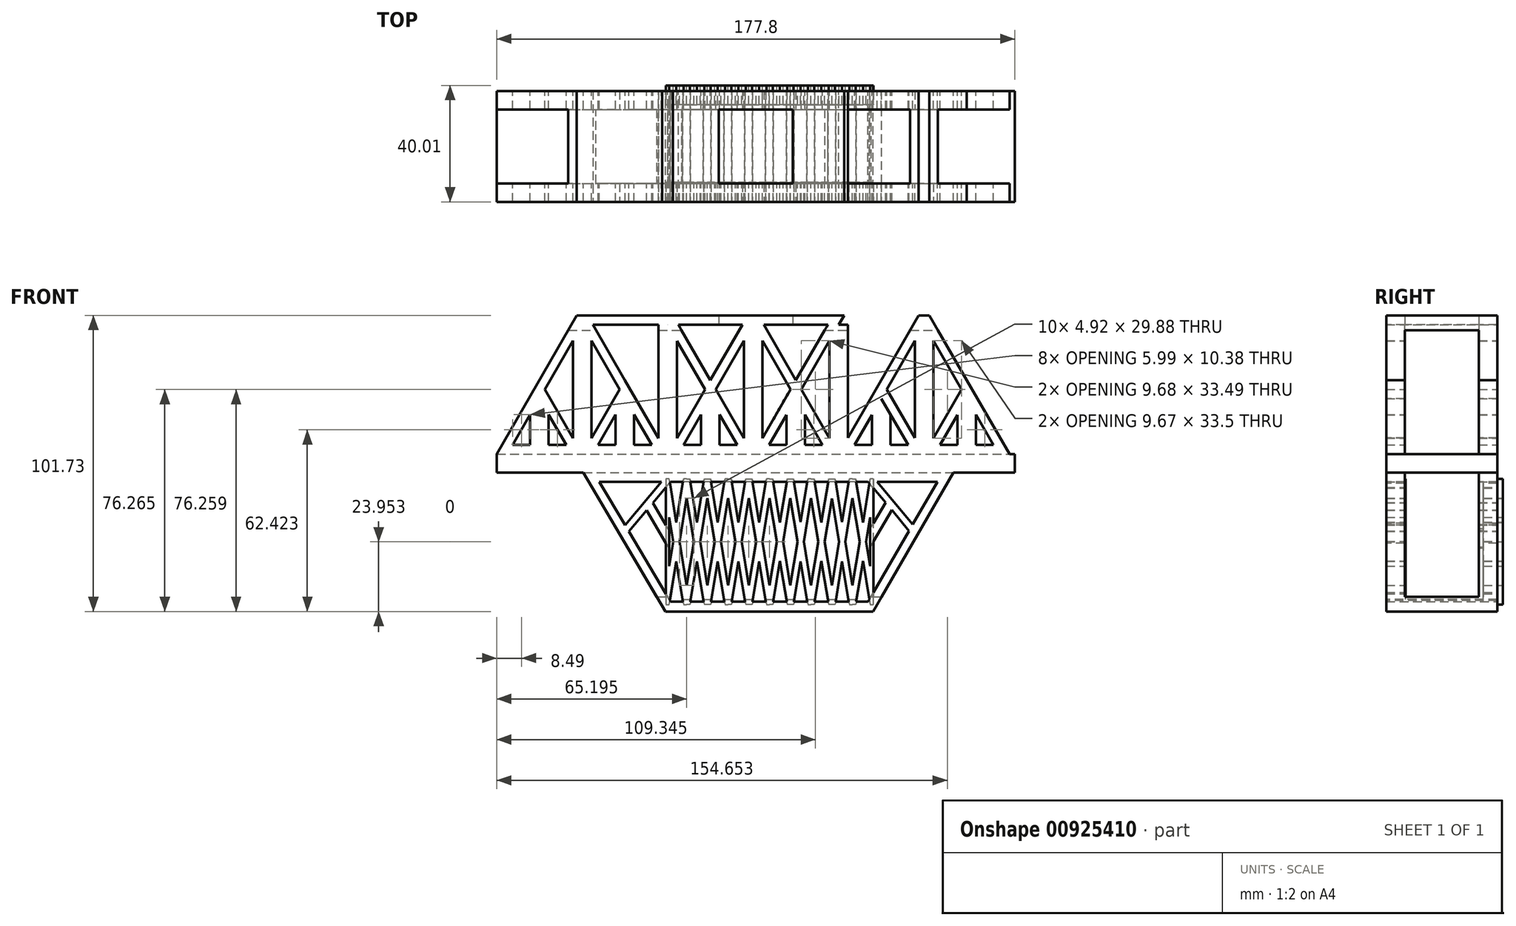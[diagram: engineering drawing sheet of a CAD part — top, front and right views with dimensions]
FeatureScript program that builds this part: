
annotation { "Feature Type Name" : "Feature", "Feature Type Description" : "" }
export const myFeature = defineFeature(function(context is Context, id is Id, definition is map)
    precondition{}
    {
        {
            var Q0;
            Q0=qCreatedBy(makeId("Front.planeOp"),FACE);
            var sketch = newSketch(context, id + "F0", { "sketchPlane" : qUnion([Q0])});
            skLineSegment(sketch, "E0.0.11", {"start": v(-111.17, 12.7) * mm, "end": v(-111.17, 0) * mm});
            skLineSegment(sketch, "E0.0.13", {"start": v(66.63, 0) * mm, "end": v(66.63, 12.7) * mm});
            skLineSegment(sketch, "E1", {"start": v(-111.17, 12.7) * mm, "end": v(66.63, 12.7) * mm});
            skLineSegment(sketch, "E2", {"start": v(66.63, 0) * mm, "end": v(-111.17, 0) * mm});
            skSolve(sketch);
        }
        {
            var Q0;
            Q0=qCreatedBy(makeId("Front.planeOp"),FACE);
            var sketch = newSketch(context, id + "F1", { "sketchPlane" : qUnion([Q0])});
            skLineSegment(sketch, "E3", {"start": v(-111.17, 0) * mm, "end": v(66.63, 0) * mm});
            skLineSegment(sketch, "E4", {"start": v(-111.17, 0) * mm, "end": v(-111.17, 12.7) * mm});
            skLineSegment(sketch, "E5", {"start": v(66.63, 12.7) * mm, "end": v(66.63, 0) * mm});
            skLineSegment(sketch, "E6", {"start": v(-111.17, 63.7) * mm, "end": v(-111.17, -37.9) * mm, "construction": true});
            skPoint(sketch, "E7.0.midPoint", {"position": v(-99.44, 28.1) * mm});
            skCircle(sketch, "E8.cCircle", {"center": v(-96.5, 21.17) * mm, "radius": 8.47 * mm, "construction": true});
            skLineSegment(sketch, "E8.0", {"start": v(-81.85, 12.7) * mm, "end": v(-111.17, 12.7) * mm});
            skLineSegment(sketch, "E8.1", {"start": v(-111.17, 12.7) * mm, "end": v(-96.5, 38.1) * mm});
            skLineSegment(sketch, "E8.2", {"start": v(-96.5, 38.1) * mm, "end": v(-81.85, 12.7) * mm});
            skLineSegment(sketch, "E9", {"start": v(-96.5, 38.1) * mm, "end": v(-96.5, 31.75) * mm, "construction": true});
            skCircle(sketch, "E10.cCircle", {"center": v(-96.5, 21.17) * mm, "radius": 5.3 * mm, "construction": true});
            skLineSegment(sketch, "E10.0", {"start": v(-87.34, 15.88) * mm, "end": v(-105.68, 15.88) * mm});
            skLineSegment(sketch, "E10.1", {"start": v(-105.68, 15.87) * mm, "end": v(-96.5, 31.75) * mm});
            skLineSegment(sketch, "E10.2", {"start": v(-96.5, 31.75) * mm, "end": v(-87.34, 15.88) * mm});
            skPoint(sketch, "E10.0.midPoint", {"position": v(-96.5, 15.88) * mm});
            skLineSegment(sketch, "E11", {"start": v(66.63, 12.7) * mm, "end": v(-111.17, 12.7) * mm});
            skLineSegment(sketch, "E12.direction1", {"start": v(-111.17, 12.7) * mm, "end": v(-81.85, 12.7) * mm, "construction": true});
            skLineSegment(sketch, "E13", {"start": v(-96.5, 38.1) * mm, "end": v(-96.5, 12.7) * mm, "construction": true});
            skLineSegment(sketch, "E14", {"start": v(-96.5, 31.75) * mm, "end": v(-93.33, 31.75) * mm, "construction": true});
            skLineSegment(sketch, "E15", {"start": v(-96.5, 31.75) * mm, "end": v(-99.68, 31.75) * mm, "construction": true});
            skLineSegment(sketch, "E16", {"start": v(-99.68, 31.75) * mm, "end": v(-99.68, 26.25) * mm, "construction": true});
            skLineSegment(sketch, "E17", {"start": v(-93.33, 31.75) * mm, "end": v(-93.33, 26.25) * mm, "construction": true});
            skLineSegment(sketch, "E18", {"start": v(-99.68, 26.25) * mm, "end": v(-99.68, 15.88) * mm});
            skLineSegment(sketch, "E19", {"start": v(-93.33, 26.25) * mm, "end": v(-93.33, 15.88) * mm});
            skLineSegment(sketch, "E20.1.0.0", {"start": v(-58, 15.88) * mm, "end": v(-76.34, 15.88) * mm});
            skLineSegment(sketch, "E20.1.0.1", {"start": v(-70.35, 26.25) * mm, "end": v(-70.35, 15.88) * mm});
            skLineSegment(sketch, "E20.1.0.2", {"start": v(-67.17, 38.1) * mm, "end": v(-52.5, 12.7) * mm});
            skPoint(sketch, "E20.1.0.3", {"position": v(-67.17, 15.88) * mm});
            skLineSegment(sketch, "E20.1.0.4", {"start": v(-67.17, 31.75) * mm, "end": v(-58, 15.88) * mm});
            skCircle(sketch, "E20.1.0.5", {"center": v(-67.17, 21.17) * mm, "radius": 8.47 * mm, "construction": true});
            skPoint(sketch, "E20.1.0.6", {"position": v(-70.1, 28.1) * mm});
            skLineSegment(sketch, "E20.1.0.7", {"start": v(-64, 26.25) * mm, "end": v(-64, 15.88) * mm});
            skLineSegment(sketch, "E20.1.0.8", {"start": v(-81.84, 12.7) * mm, "end": v(-52.5, 12.7) * mm, "construction": true});
            skLineSegment(sketch, "E20.1.0.9", {"start": v(-76.34, 15.87) * mm, "end": v(-67.17, 31.75) * mm});
            skCircle(sketch, "E20.1.0.10", {"center": v(-67.17, 21.17) * mm, "radius": 5.3 * mm, "construction": true});
            skLineSegment(sketch, "E20.1.0.11", {"start": v(-81.84, 12.7) * mm, "end": v(-67.17, 38.1) * mm});
            skLineSegment(sketch, "E20.1.0.12", {"start": v(-64, 31.75) * mm, "end": v(-64, 26.25) * mm, "construction": true});
            skLineSegment(sketch, "E20.1.0.13", {"start": v(-67.17, 38.1) * mm, "end": v(-67.17, 12.7) * mm, "construction": true});
            skLineSegment(sketch, "E20.1.0.14", {"start": v(-52.5, 12.7) * mm, "end": v(-81.84, 12.7) * mm});
            skLineSegment(sketch, "E20.1.0.15", {"start": v(-67.17, 38.1) * mm, "end": v(-67.17, 31.75) * mm, "construction": true});
            skLineSegment(sketch, "E20.1.0.16", {"start": v(-70.35, 31.75) * mm, "end": v(-70.35, 26.25) * mm, "construction": true});
            skLineSegment(sketch, "E20.1.0.17", {"start": v(-67.17, 31.75) * mm, "end": v(-70.35, 31.75) * mm, "construction": true});
            skLineSegment(sketch, "E20.1.0.18", {"start": v(-67.17, 31.75) * mm, "end": v(-64, 31.75) * mm, "construction": true});
            skLineSegment(sketch, "E20.direction1", {"start": v(-111.17, 12.7) * mm, "end": v(-81.84, 12.7) * mm, "construction": true});
            skLineSegment(sketch, "E21", {"start": v(-52.5, 12.7) * mm, "end": v(-52.5, 29.72) * mm, "construction": true});
            skLineSegment(sketch, "E22.MirrorCS", {"start": v(-37.84, 31.75) * mm, "end": v(-34.67, 31.75) * mm, "construction": true});
            skLineSegment(sketch, "E23.MirrorCS", {"start": v(-37.84, 31.75) * mm, "end": v(-41.02, 31.75) * mm, "construction": true});
            skLineSegment(sketch, "E24.MirrorCS", {"start": v(-37.84, 38.1) * mm, "end": v(-37.84, 31.75) * mm, "construction": true});
            skLineSegment(sketch, "E25.MirrorCS", {"start": v(-34.67, 31.75) * mm, "end": v(-34.67, 26.25) * mm, "construction": true});
            skLineSegment(sketch, "E26.MirrorCS", {"start": v(-41.02, 31.75) * mm, "end": v(-41.02, 26.25) * mm, "construction": true});
            skLineSegment(sketch, "E27.MirrorCS", {"start": v(-34.67, 26.25) * mm, "end": v(-34.67, 15.88) * mm});
            skLineSegment(sketch, "E28.MirrorCS", {"start": v(-37.84, 38.1) * mm, "end": v(-37.84, 12.7) * mm, "construction": true});
            skLineSegment(sketch, "E29.MirrorCS", {"start": v(-47, 15.88) * mm, "end": v(-28.68, 15.88) * mm});
            skPoint(sketch, "E30.MirrorP", {"position": v(-37.84, 15.88) * mm});
            skLineSegment(sketch, "E31.MirrorCS", {"start": v(-23.18, 12.7) * mm, "end": v(-37.84, 38.1) * mm});
            skLineSegment(sketch, "E32.MirrorCS", {"start": v(-41.02, 26.25) * mm, "end": v(-41.02, 15.88) * mm});
            skCircle(sketch, "E33.MirrorC", {"center": v(-37.84, 21.17) * mm, "radius": 8.47 * mm, "construction": true});
            skLineSegment(sketch, "E34.MirrorCS", {"start": v(-28.68, 15.87) * mm, "end": v(-37.84, 31.75) * mm});
            skPoint(sketch, "E35.MirrorP", {"position": v(-34.91, 28.1) * mm});
            skCircle(sketch, "E36.MirrorC", {"center": v(-37.84, 21.17) * mm, "radius": 5.3 * mm, "construction": true});
            skLineSegment(sketch, "E37.MirrorCS", {"start": v(-37.84, 31.75) * mm, "end": v(-47, 15.88) * mm});
            skLineSegment(sketch, "E38.MirrorCS", {"start": v(-37.84, 38.1) * mm, "end": v(-52.5, 12.7) * mm});
            skLineSegment(sketch, "E39", {"start": v(-23.17, 12.7) * mm, "end": v(-23.17, 25.04) * mm, "construction": true});
            skLineSegment(sketch, "E40.MirrorCS", {"start": v(50.17, 31.75) * mm, "end": v(53.34, 31.75) * mm, "construction": true});
            skLineSegment(sketch, "E41.MirrorCS", {"start": v(50.17, 31.75) * mm, "end": v(47, 31.75) * mm, "construction": true});
            skLineSegment(sketch, "E42.MirrorCS", {"start": v(47, 31.75) * mm, "end": v(47, 26.25) * mm, "construction": true});
            skLineSegment(sketch, "E43.MirrorCS", {"start": v(-5.32, 31.75) * mm, "end": v(-5.32, 26.25) * mm, "construction": true});
            skLineSegment(sketch, "E44.MirrorCS", {"start": v(53.34, 31.75) * mm, "end": v(53.34, 26.25) * mm, "construction": true});
            skLineSegment(sketch, "E45.MirrorCS", {"start": v(-8.5, 31.75) * mm, "end": v(-5.32, 31.75) * mm, "construction": true});
            skLineSegment(sketch, "E46.MirrorCS", {"start": v(35.5, 12.7) * mm, "end": v(64.83, 12.7) * mm});
            skLineSegment(sketch, "E47.MirrorCS", {"start": v(-8.5, 31.75) * mm, "end": v(-11.67, 31.75) * mm, "construction": true});
            skLineSegment(sketch, "E48.MirrorCS", {"start": v(-11.67, 31.75) * mm, "end": v(-11.67, 26.25) * mm, "construction": true});
            skLineSegment(sketch, "E49.MirrorCS", {"start": v(0.67, 15.88) * mm, "end": v(-17.66, 15.88) * mm});
            skLineSegment(sketch, "E50.MirrorCS", {"start": v(64.83, 12.7) * mm, "end": v(35.5, 12.7) * mm, "construction": true});
            skLineSegment(sketch, "E51.MirrorCS", {"start": v(64.83, 0) * mm, "end": v(64.83, 12.7) * mm});
            skLineSegment(sketch, "E52.MirrorCS", {"start": v(50.17, 38.1) * mm, "end": v(50.17, 31.75) * mm, "construction": true});
            skLineSegment(sketch, "E53.MirrorCS", {"start": v(41, 15.88) * mm, "end": v(59.33, 15.88) * mm});
            skLineSegment(sketch, "E54.MirrorCS", {"start": v(-8.5, 38.1) * mm, "end": v(-8.5, 31.75) * mm, "construction": true});
            skLineSegment(sketch, "E55.MirrorCS", {"start": v(-17.66, 15.88) * mm, "end": v(-8.5, 31.75) * mm});
            skLineSegment(sketch, "E56.MirrorCS", {"start": v(-11.67, 26.25) * mm, "end": v(-11.67, 15.88) * mm});
            skLineSegment(sketch, "E57.MirrorCS", {"start": v(-23.16, 12.7) * mm, "end": v(-8.5, 38.1) * mm});
            skCircle(sketch, "E58.MirrorC", {"center": v(50.17, 21.17) * mm, "radius": 5.3 * mm, "construction": true});
            skLineSegment(sketch, "E59.MirrorCS", {"start": v(50.17, 38.1) * mm, "end": v(35.5, 12.7) * mm});
            skPoint(sketch, "E60.MirrorP", {"position": v(-8.5, 15.88) * mm});
            skLineSegment(sketch, "E61.MirrorCS", {"start": v(50.17, 31.75) * mm, "end": v(41, 15.88) * mm});
            skCircle(sketch, "E62.MirrorC", {"center": v(50.17, 21.17) * mm, "radius": 8.47 * mm, "construction": true});
            skLineSegment(sketch, "E63.MirrorCS", {"start": v(50.17, 38.1) * mm, "end": v(50.17, 12.7) * mm, "construction": true});
            skLineSegment(sketch, "E64.MirrorCS", {"start": v(-8.5, 38.1) * mm, "end": v(-8.5, 12.7) * mm, "construction": true});
            skCircle(sketch, "E65.MirrorC", {"center": v(-8.5, 21.17) * mm, "radius": 5.3 * mm, "construction": true});
            skLineSegment(sketch, "E66.MirrorCS", {"start": v(-5.32, 26.25) * mm, "end": v(-5.32, 15.88) * mm});
            skCircle(sketch, "E67.MirrorC", {"center": v(-8.5, 21.17) * mm, "radius": 8.47 * mm, "construction": true});
            skLineSegment(sketch, "E68.MirrorCS", {"start": v(53.34, 26.25) * mm, "end": v(53.34, 15.88) * mm});
            skPoint(sketch, "E69.MirrorP", {"position": v(-11.43, 28.1) * mm});
            skPoint(sketch, "E70.MirrorP", {"position": v(53.1, 28.1) * mm});
            skLineSegment(sketch, "E71.MirrorCS", {"start": v(-8.5, 31.75) * mm, "end": v(0.67, 15.88) * mm});
            skLineSegment(sketch, "E72.MirrorCS", {"start": v(47, 26.25) * mm, "end": v(47, 15.88) * mm});
            skLineSegment(sketch, "E73.MirrorCS", {"start": v(64.83, 12.7) * mm, "end": v(50.17, 38.1) * mm});
            skLineSegment(sketch, "E74.MirrorCS", {"start": v(-8.5, 38.1) * mm, "end": v(6.17, 12.7) * mm});
            skLineSegment(sketch, "E75.MirrorCS", {"start": v(59.33, 15.88) * mm, "end": v(50.17, 31.75) * mm});
            skPoint(sketch, "E76.MirrorP", {"position": v(50.17, 15.88) * mm});
            skLineSegment(sketch, "E77.MirrorCS", {"start": v(6.18, 12.7) * mm, "end": v(20.85, 38.1) * mm});
            skLineSegment(sketch, "E78.MirrorCS", {"start": v(20.85, 38.1) * mm, "end": v(35.51, 12.7) * mm});
            skLineSegment(sketch, "E79.MirrorCS", {"start": v(20.85, 38.1) * mm, "end": v(20.85, 31.75) * mm, "construction": true});
            skLineSegment(sketch, "E80.MirrorCS", {"start": v(20.85, 31.75) * mm, "end": v(24.02, 31.75) * mm, "construction": true});
            skLineSegment(sketch, "E81.MirrorCS", {"start": v(20.85, 31.75) * mm, "end": v(17.67, 31.75) * mm, "construction": true});
            skLineSegment(sketch, "E82.MirrorCS", {"start": v(24.02, 31.75) * mm, "end": v(24.02, 26.25) * mm, "construction": true});
            skLineSegment(sketch, "E83.MirrorCS", {"start": v(20.85, 31.75) * mm, "end": v(30.01, 15.88) * mm});
            skCircle(sketch, "E84.MirrorC", {"center": v(20.85, 21.17) * mm, "radius": 8.47 * mm, "construction": true});
            skLineSegment(sketch, "E85.MirrorCS", {"start": v(20.85, 38.1) * mm, "end": v(20.85, 12.7) * mm, "construction": true});
            skLineSegment(sketch, "E86.MirrorCS", {"start": v(11.68, 15.88) * mm, "end": v(20.85, 31.75) * mm});
            skLineSegment(sketch, "E87.MirrorCS", {"start": v(17.67, 31.75) * mm, "end": v(17.67, 26.25) * mm, "construction": true});
            skLineSegment(sketch, "E88.MirrorCS", {"start": v(17.67, 26.25) * mm, "end": v(17.67, 15.88) * mm});
            skCircle(sketch, "E89.MirrorC", {"center": v(20.85, 21.17) * mm, "radius": 5.3 * mm, "construction": true});
            skLineSegment(sketch, "E90.MirrorCS", {"start": v(24.02, 26.25) * mm, "end": v(24.02, 15.88) * mm});
            skLineSegment(sketch, "E91.MirrorCS", {"start": v(30.01, 15.88) * mm, "end": v(11.68, 15.88) * mm});
            skSolve(sketch);
        }
        {
            var Q0;
            Q0=qCreatedBy(makeId("Front.planeOp"),FACE);
            var sketch = newSketch(context, id + "F2", { "sketchPlane" : qUnion([Q0])});
            skCircle(sketch, "E92.cCircle", {"center": v(-81.85, 29.63) * mm, "radius": 16.93 * mm, "construction": true});
            skLineSegment(sketch, "E92.2", {"start": v(-81.85, 63.5) * mm, "end": v(-52.52, 12.7) * mm});
            skPoint(sketch, "E92.0.midPoint", {"position": v(-81.85, 12.7) * mm});
            skLineSegment(sketch, "E93.0.5", {"start": v(-81.85, 12.7) * mm, "end": v(-111.17, 12.7) * mm});
            skLineSegment(sketch, "E93.0.6", {"start": v(-111.17, 12.7) * mm, "end": v(-111.17, 0) * mm});
            skLineSegment(sketch, "E93.0.7", {"start": v(-111.17, 0) * mm, "end": v(66.63, 0) * mm});
            skLineSegment(sketch, "E93.0.8", {"start": v(66.63, 0) * mm, "end": v(66.63, 12.7) * mm});
            skLineSegment(sketch, "E94.0.1", {"start": v(-96.52, 31.75) * mm, "end": v(-105.69, 15.88) * mm, "construction": true});
            skLineSegment(sketch, "E94.0.2", {"start": v(-105.69, 15.88) * mm, "end": v(-87.36, 15.88) * mm, "construction": true});
            skLineSegment(sketch, "E95.0.1", {"start": v(-81.85, 12.7) * mm, "end": v(-96.5, 38.1) * mm, "construction": true});
            skLineSegment(sketch, "E95.0.2", {"start": v(-96.5, 38.1) * mm, "end": v(-111.17, 12.7) * mm, "construction": true});
            skCircle(sketch, "E96.cCircle", {"center": v(-81.85, 29.63) * mm, "radius": 13.76 * mm, "construction": true});
            skLineSegment(sketch, "E96.0", {"start": v(-81.85, 57.15) * mm, "end": v(-105.68, 15.88) * mm});
            skLineSegment(sketch, "E96.1", {"start": v(-58.02, 15.87) * mm, "end": v(-81.85, 57.15) * mm});
            skLineSegment(sketch, "E96.2", {"start": v(-105.68, 15.88) * mm, "end": v(-58.02, 15.88) * mm});
            skPoint(sketch, "E96.0.midPoint", {"position": v(-93.76, 36.51) * mm});
            skLineSegment(sketch, "E97", {"start": v(-81.85, 63.5) * mm, "end": v(-81.85, 57.15) * mm, "construction": true});
            skLineSegment(sketch, "E98", {"start": v(-81.85, 29.63) * mm, "end": v(-81.85, 57.15) * mm, "construction": true});
            skLineSegment(sketch, "E99", {"start": v(-81.85, 57.15) * mm, "end": v(-78.67, 57.15) * mm, "construction": true});
            skLineSegment(sketch, "E100", {"start": v(-81.85, 57.15) * mm, "end": v(-85.02, 57.15) * mm, "construction": true});
            skLineSegment(sketch, "E101", {"start": v(-78.67, 57.15) * mm, "end": v(-78.67, 51.65) * mm, "construction": true});
            skLineSegment(sketch, "E102", {"start": v(-85.02, 57.15) * mm, "end": v(-85.02, 51.65) * mm, "construction": true});
            skLineSegment(sketch, "E103", {"start": v(-85.02, 51.65) * mm, "end": v(-85.02, 15.88) * mm});
            skLineSegment(sketch, "E104", {"start": v(-78.67, 51.65) * mm, "end": v(-78.67, 15.88) * mm});
            skLineSegment(sketch, "E105", {"start": v(-81.85, 12.7) * mm, "end": v(-52.52, 12.7) * mm});
            skPoint(sketch, "E106.1.0.0", {"position": v(-35.1, 36.51) * mm});
            skLineSegment(sketch, "E106.1.0.1", {"start": v(-47.02, 15.88) * mm, "end": v(0.64, 15.88) * mm});
            skLineSegment(sketch, "E106.1.0.3", {"start": v(-23.19, 12.7) * mm, "end": v(-37.85, 38.1) * mm, "construction": true});
            skLineSegment(sketch, "E106.1.0.4", {"start": v(0.64, 15.88) * mm, "end": v(-23.19, 57.15) * mm});
            skLineSegment(sketch, "E106.1.0.5", {"start": v(-23.19, 57.15) * mm, "end": v(-47.02, 15.88) * mm});
            skLineSegment(sketch, "E106.1.0.6", {"start": v(-23.19, 63.5) * mm, "end": v(6.14, 12.7) * mm});
            skLineSegment(sketch, "E106.1.0.7", {"start": v(-23.19, 29.63) * mm, "end": v(-23.19, 57.15) * mm, "construction": true});
            skLineSegment(sketch, "E106.1.0.8", {"start": v(-20.01, 57.15) * mm, "end": v(-20.01, 51.65) * mm, "construction": true});
            skLineSegment(sketch, "E106.1.0.9", {"start": v(-37.85, 38.1) * mm, "end": v(-52.52, 12.7) * mm, "construction": true});
            skLineSegment(sketch, "E106.1.0.10", {"start": v(-23.19, 63.5) * mm, "end": v(-23.19, 57.15) * mm, "construction": true});
            skLineSegment(sketch, "E106.1.0.11", {"start": v(-47.03, 15.88) * mm, "end": v(-28.7, 15.88) * mm, "construction": true});
            skCircle(sketch, "E106.1.0.12", {"center": v(-23.19, 29.63) * mm, "radius": 13.76 * mm, "construction": true});
            skLineSegment(sketch, "E106.1.0.13", {"start": v(-23.19, 12.7) * mm, "end": v(6.14, 12.7) * mm});
            skLineSegment(sketch, "E106.1.0.14", {"start": v(-26.36, 57.15) * mm, "end": v(-26.36, 51.65) * mm, "construction": true});
            skCircle(sketch, "E106.1.0.15", {"center": v(-23.19, 29.63) * mm, "radius": 16.93 * mm, "construction": true});
            skPoint(sketch, "E106.1.0.16", {"position": v(-23.19, 12.7) * mm});
            skLineSegment(sketch, "E106.1.0.17", {"start": v(-37.86, 31.75) * mm, "end": v(-47.03, 15.88) * mm, "construction": true});
            skLineSegment(sketch, "E106.1.0.18", {"start": v(-26.36, 51.65) * mm, "end": v(-26.36, 15.88) * mm});
            skLineSegment(sketch, "E106.1.0.19", {"start": v(-20.01, 51.65) * mm, "end": v(-20.01, 15.88) * mm});
            skLineSegment(sketch, "E106.1.0.20", {"start": v(-23.19, 12.7) * mm, "end": v(-52.52, 12.7) * mm});
            skLineSegment(sketch, "E106.1.0.21", {"start": v(-23.19, 57.15) * mm, "end": v(-20.01, 57.15) * mm, "construction": true});
            skLineSegment(sketch, "E106.1.0.22", {"start": v(-23.19, 57.15) * mm, "end": v(-26.36, 57.15) * mm, "construction": true});
            skPoint(sketch, "E106.2.0.0", {"position": v(23.56, 36.51) * mm});
            skLineSegment(sketch, "E106.2.0.1", {"start": v(11.64, 15.88) * mm, "end": v(59.3, 15.88) * mm});
            skLineSegment(sketch, "E106.2.0.3", {"start": v(35.47, 12.7) * mm, "end": v(20.8, 38.1) * mm, "construction": true});
            skLineSegment(sketch, "E106.2.0.4", {"start": v(59.3, 15.88) * mm, "end": v(35.47, 57.15) * mm});
            skLineSegment(sketch, "E106.2.0.5", {"start": v(35.47, 57.15) * mm, "end": v(11.64, 15.88) * mm});
            skLineSegment(sketch, "E106.2.0.6", {"start": v(35.47, 63.5) * mm, "end": v(64.8, 12.7) * mm});
            skLineSegment(sketch, "E106.2.0.7", {"start": v(35.47, 29.63) * mm, "end": v(35.47, 57.15) * mm, "construction": true});
            skLineSegment(sketch, "E106.2.0.8", {"start": v(38.65, 57.15) * mm, "end": v(38.65, 51.65) * mm, "construction": true});
            skLineSegment(sketch, "E106.2.0.9", {"start": v(20.8, 38.1) * mm, "end": v(6.14, 12.7) * mm, "construction": true});
            skLineSegment(sketch, "E106.2.0.10", {"start": v(35.47, 63.5) * mm, "end": v(35.47, 57.15) * mm, "construction": true});
            skLineSegment(sketch, "E106.2.0.11", {"start": v(11.63, 15.88) * mm, "end": v(29.96, 15.88) * mm, "construction": true});
            skCircle(sketch, "E106.2.0.12", {"center": v(35.47, 29.63) * mm, "radius": 13.76 * mm, "construction": true});
            skLineSegment(sketch, "E106.2.0.13", {"start": v(35.47, 12.7) * mm, "end": v(64.8, 12.7) * mm});
            skLineSegment(sketch, "E106.2.0.14", {"start": v(32.3, 57.15) * mm, "end": v(32.3, 51.65) * mm, "construction": true});
            skCircle(sketch, "E106.2.0.15", {"center": v(35.47, 29.63) * mm, "radius": 16.93 * mm, "construction": true});
            skPoint(sketch, "E106.2.0.16", {"position": v(35.47, 12.7) * mm});
            skLineSegment(sketch, "E106.2.0.17", {"start": v(20.8, 31.75) * mm, "end": v(11.63, 15.88) * mm, "construction": true});
            skLineSegment(sketch, "E106.2.0.18", {"start": v(32.3, 51.65) * mm, "end": v(32.3, 15.88) * mm});
            skLineSegment(sketch, "E106.2.0.19", {"start": v(38.65, 51.65) * mm, "end": v(38.65, 15.88) * mm});
            skLineSegment(sketch, "E106.2.0.20", {"start": v(35.47, 12.7) * mm, "end": v(6.14, 12.7) * mm});
            skLineSegment(sketch, "E106.2.0.21", {"start": v(35.47, 57.15) * mm, "end": v(38.65, 57.15) * mm, "construction": true});
            skLineSegment(sketch, "E106.2.0.22", {"start": v(35.47, 57.15) * mm, "end": v(32.3, 57.15) * mm, "construction": true});
            skLineSegment(sketch, "E106.direction1", {"start": v(-111.17, 12.7) * mm, "end": v(-52.52, 12.7) * mm, "construction": true});
            skLineSegment(sketch, "E107", {"start": v(-81.85, 60.33) * mm, "end": v(-80.01, 60.33) * mm});
            skLineSegment(sketch, "E108", {"start": v(-81.85, 60.33) * mm, "end": v(-83.68, 60.33) * mm});
            skLineSegment(sketch, "E109", {"start": v(-83.68, 60.33) * mm, "end": v(-111.17, 12.7) * mm});
            skLineSegment(sketch, "E110", {"start": v(-23.19, 60.33) * mm, "end": v(-25.02, 60.33) * mm});
            skLineSegment(sketch, "E111", {"start": v(-23.19, 60.33) * mm, "end": v(-21.35, 60.33) * mm});
            skLineSegment(sketch, "E112", {"start": v(-25.02, 60.33) * mm, "end": v(-52.52, 12.7) * mm});
            skLineSegment(sketch, "E113", {"start": v(35.47, 60.33) * mm, "end": v(33.64, 60.33) * mm});
            skLineSegment(sketch, "E114", {"start": v(35.47, 60.33) * mm, "end": v(37.3, 60.33) * mm});
            skLineSegment(sketch, "E115", {"start": v(33.64, 60.33) * mm, "end": v(6.14, 12.7) * mm});
            skLineSegment(sketch, "E116", {"start": v(66.63, 12.7) * mm, "end": v(64.8, 12.7) * mm});
            skSolve(sketch);
        }
        {
            var Q0;
            Q0=qCreatedBy(makeId("Front.planeOp"),FACE);
            var sketch = newSketch(context, id + "F3", { "sketchPlane" : qUnion([Q0])});
            skLineSegment(sketch, "E117.0.0", {"start": v(-78.67, 15.88) * mm, "end": v(-78.67, 51.65) * mm});
            skLineSegment(sketch, "E117.0.1", {"start": v(-78.67, 51.65) * mm, "end": v(-81.85, 57.15) * mm});
            skLineSegment(sketch, "E117.0.2", {"start": v(-81.85, 57.15) * mm, "end": v(-85.02, 51.65) * mm});
            skLineSegment(sketch, "E117.0.3", {"start": v(-85.02, 51.65) * mm, "end": v(-85.02, 15.88) * mm});
            skLineSegment(sketch, "E118.0.0", {"start": v(-93.33, 15.88) * mm, "end": v(-93.33, 26.25) * mm});
            skLineSegment(sketch, "E118.0.1", {"start": v(-93.33, 26.25) * mm, "end": v(-96.5, 31.75) * mm});
            skLineSegment(sketch, "E118.0.2", {"start": v(-96.5, 31.75) * mm, "end": v(-99.68, 26.25) * mm});
            skLineSegment(sketch, "E118.0.3", {"start": v(-99.68, 26.25) * mm, "end": v(-99.68, 15.88) * mm});
            skLineSegment(sketch, "E118.0.4", {"start": v(-99.68, 15.88) * mm, "end": v(-93.33, 15.88) * mm});
            skLineSegment(sketch, "E119.MirrorCS", {"start": v(-70.36, 26.25) * mm, "end": v(-67.18, 31.75) * mm});
            skLineSegment(sketch, "E120.MirrorCS", {"start": v(-70.36, 15.88) * mm, "end": v(-70.36, 26.25) * mm});
            skLineSegment(sketch, "E121.MirrorCS", {"start": v(-64, 15.88) * mm, "end": v(-70.36, 15.88) * mm});
            skLineSegment(sketch, "E122.MirrorCS", {"start": v(-64, 26.25) * mm, "end": v(-64, 15.88) * mm});
            skLineSegment(sketch, "E123.MirrorCS", {"start": v(-67.18, 31.75) * mm, "end": v(-64, 26.25) * mm});
            skLineSegment(sketch, "E124", {"start": v(-36.02, 34.98) * mm, "end": v(-50.7, 60.37) * mm});
            skLineSegment(sketch, "E125.MirrorCS", {"start": v(-10.35, 34.98) * mm, "end": v(4.33, 60.37) * mm});
            skLineSegment(sketch, "E126", {"start": v(-50.7, 60.37) * mm, "end": v(4.33, 60.37) * mm, "construction": true});
            skLineSegment(sketch, "E127", {"start": v(-52.52, 12.7) * mm, "end": v(-52.52, 27.16) * mm, "construction": true});
            skLineSegment(sketch, "E128.MirrorCS", {"start": v(-41.03, 26.25) * mm, "end": v(-41.03, 15.87) * mm});
            skLineSegment(sketch, "E129.MirrorCS", {"start": v(-37.85, 31.75) * mm, "end": v(-41.03, 26.25) * mm});
            skLineSegment(sketch, "E130.MirrorCS", {"start": v(-34.68, 26.25) * mm, "end": v(-37.85, 31.75) * mm});
            skLineSegment(sketch, "E131.MirrorCS", {"start": v(-34.68, 15.88) * mm, "end": v(-34.68, 26.25) * mm});
            skLineSegment(sketch, "E132.MirrorCS", {"start": v(-41.03, 15.88) * mm, "end": v(-34.68, 15.88) * mm});
            skLineSegment(sketch, "E133.MirrorCS", {"start": v(-26.36, 51.65) * mm, "end": v(-23.19, 57.15) * mm});
            skPoint(sketch, "E134.MirrorP", {"position": v(-23.19, 63.5) * mm});
            skLineSegment(sketch, "E135.MirrorCS", {"start": v(35.47, 57.15) * mm, "end": v(38.65, 51.65) * mm});
            skLineSegment(sketch, "E136.MirrorCS", {"start": v(32.3, 51.65) * mm, "end": v(35.47, 57.15) * mm});
            skLineSegment(sketch, "E137.MirrorCS", {"start": v(35.47, 15.88) * mm, "end": v(38.65, 15.88) * mm});
            skLineSegment(sketch, "E138.MirrorCS", {"start": v(32.3, 15.88) * mm, "end": v(35.47, 15.88) * mm});
            skLineSegment(sketch, "E139.MirrorCS", {"start": v(17.63, 15.88) * mm, "end": v(23.98, 15.88) * mm});
            skLineSegment(sketch, "E140.MirrorCS", {"start": v(53.31, 15.88) * mm, "end": v(46.96, 15.88) * mm});
            skLineSegment(sketch, "E141.MirrorCS", {"start": v(23.98, 26.25) * mm, "end": v(20.8, 31.75) * mm});
            skLineSegment(sketch, "E142.MirrorCS", {"start": v(20.8, 31.75) * mm, "end": v(17.63, 26.25) * mm});
            skLineSegment(sketch, "E143.MirrorCS", {"start": v(50.14, 31.75) * mm, "end": v(53.31, 26.25) * mm});
            skLineSegment(sketch, "E144.MirrorCS", {"start": v(46.96, 26.25) * mm, "end": v(50.14, 31.75) * mm});
            skLineSegment(sketch, "E145.MirrorCS", {"start": v(32.3, 15.88) * mm, "end": v(32.3, 51.65) * mm});
            skLineSegment(sketch, "E146.MirrorCS", {"start": v(53.31, 26.25) * mm, "end": v(53.31, 15.88) * mm});
            skLineSegment(sketch, "E147.MirrorCS", {"start": v(17.63, 26.25) * mm, "end": v(17.63, 15.88) * mm});
            skLineSegment(sketch, "E148.MirrorCS", {"start": v(23.98, 15.88) * mm, "end": v(23.98, 26.25) * mm});
            skLineSegment(sketch, "E149.MirrorCS", {"start": v(46.96, 15.88) * mm, "end": v(46.96, 26.25) * mm});
            skLineSegment(sketch, "E150.MirrorCS", {"start": v(38.65, 51.65) * mm, "end": v(38.65, 15.88) * mm});
            skLineSegment(sketch, "E151.MirrorCS", {"start": v(-5.35, 26.25) * mm, "end": v(-5.35, 15.87) * mm});
            skLineSegment(sketch, "E152.MirrorCS", {"start": v(-8.52, 31.75) * mm, "end": v(-5.35, 26.25) * mm});
            skLineSegment(sketch, "E153.MirrorCS", {"start": v(-5.35, 15.88) * mm, "end": v(-11.7, 15.88) * mm});
            skLineSegment(sketch, "E154.MirrorCS", {"start": v(-11.7, 15.88) * mm, "end": v(-11.7, 26.25) * mm});
            skLineSegment(sketch, "E155.MirrorCS", {"start": v(-11.7, 26.25) * mm, "end": v(-8.52, 31.75) * mm});
            skLineSegment(sketch, "E156.MirrorCS", {"start": v(-20.01, 51.65) * mm, "end": v(-23.19, 57.15) * mm});
            skLineSegment(sketch, "E157.0", {"start": v(-28.68, 15.87) * mm, "end": v(-37.84, 31.75) * mm});
            skLineSegment(sketch, "E158.0", {"start": v(-23.18, 12.7) * mm, "end": v(-37.84, 38.1) * mm});
            skLineSegment(sketch, "E159", {"start": v(-37.84, 31.75) * mm, "end": v(-54.36, 60.33) * mm});
            skLineSegment(sketch, "E160.0", {"start": v(-17.66, 15.88) * mm, "end": v(-8.5, 31.75) * mm});
            skLineSegment(sketch, "E160.1", {"start": v(-23.16, 12.7) * mm, "end": v(-8.5, 38.1) * mm});
            skLineSegment(sketch, "E161", {"start": v(-17.66, 15.88) * mm, "end": v(-21.33, 15.87) * mm});
            skLineSegment(sketch, "E162", {"start": v(-54.36, 60.33) * mm, "end": v(-50.7, 60.37) * mm});
            skLineSegment(sketch, "E163", {"start": v(4.33, 60.37) * mm, "end": v(8.03, 60.37) * mm});
            skLineSegment(sketch, "E164", {"start": v(-21.33, 15.87) * mm, "end": v(-23.19, 15.88) * mm});
            skLineSegment(sketch, "E165", {"start": v(-21.33, 15.87) * mm, "end": v(-20.01, 18.16) * mm});
            skLineSegment(sketch, "E166", {"start": v(-20.01, 18.16) * mm, "end": v(-20.01, 51.65) * mm});
            skLineSegment(sketch, "E167", {"start": v(-23.19, 15.88) * mm, "end": v(-25.01, 15.87) * mm});
            skLineSegment(sketch, "E168", {"start": v(-25.01, 15.87) * mm, "end": v(-26.36, 18.21) * mm});
            skLineSegment(sketch, "E169", {"start": v(-26.36, 51.65) * mm, "end": v(-26.36, 18.21) * mm});
            skLineSegment(sketch, "E170", {"start": v(-28.68, 15.87) * mm, "end": v(-25.01, 15.88) * mm});
            skLineSegment(sketch, "E171", {"start": v(-25.01, 15.87) * mm, "end": v(-50.7, 60.37) * mm});
            skLineSegment(sketch, "E172", {"start": v(-21.33, 15.87) * mm, "end": v(-17.66, 15.88) * mm});
            skLineSegment(sketch, "E173", {"start": v(-21.33, 15.87) * mm, "end": v(4.33, 60.37) * mm});
            skLineSegment(sketch, "E174.0", {"start": v(-78.67, 57.15) * mm, "end": v(-78.67, 51.65) * mm, "construction": true});
            skLineSegment(sketch, "E175.0", {"start": v(-81.85, 57.15) * mm, "end": v(-78.67, 57.15) * mm, "construction": true});
            skLineSegment(sketch, "E176.0", {"start": v(-81.85, 57.15) * mm, "end": v(-85.02, 57.15) * mm, "construction": true});
            skLineSegment(sketch, "E177.0", {"start": v(-85.02, 57.15) * mm, "end": v(-85.02, 51.65) * mm, "construction": true});
            skLineSegment(sketch, "E178.MirrorCS", {"start": v(-55.68, 15.88) * mm, "end": v(-55.68, 51.65) * mm});
            skLineSegment(sketch, "E179.MirrorCS", {"start": v(-49.33, 51.65) * mm, "end": v(-49.33, 15.88) * mm});
            skLineSegment(sketch, "E180.MirrorCS", {"start": v(-52.5, 57.15) * mm, "end": v(-49.33, 51.65) * mm});
            skLineSegment(sketch, "E181.MirrorCS", {"start": v(-55.68, 51.65) * mm, "end": v(-52.5, 57.15) * mm});
            skLineSegment(sketch, "E182.MirrorCS", {"start": v(-52.5, 57.15) * mm, "end": v(-55.68, 57.15) * mm});
            skLineSegment(sketch, "E183.MirrorCS", {"start": v(-55.68, 57.15) * mm, "end": v(-55.68, 51.65) * mm});
            skLineSegment(sketch, "E184", {"start": v(-85.02, 15.88) * mm, "end": v(-85.02, 12.7) * mm});
            skLineSegment(sketch, "E185", {"start": v(-78.67, 15.88) * mm, "end": v(-78.67, 12.7) * mm});
            skLineSegment(sketch, "E186", {"start": v(-78.67, 12.7) * mm, "end": v(-85.02, 12.7) * mm});
            skLineSegment(sketch, "E187.MirrorCS", {"start": v(-55.68, 15.88) * mm, "end": v(-55.68, 12.7) * mm});
            skLineSegment(sketch, "E188.MirrorCS", {"start": v(-49.33, 15.88) * mm, "end": v(-49.33, 12.7) * mm});
            skLineSegment(sketch, "E189.MirrorCS", {"start": v(-55.68, 12.7) * mm, "end": v(-49.33, 12.7) * mm});
            skLineSegment(sketch, "E190", {"start": v(-81.92, 60.33) * mm, "end": v(-54.36, 60.33) * mm});
            skLineSegment(sketch, "E191", {"start": v(-78.67, 57.15) * mm, "end": v(-55.68, 57.15) * mm});
            skLineSegment(sketch, "E192", {"start": v(-48.83, 57.15) * mm, "end": v(2.46, 57.15) * mm, "construction": true});
            skPoint(sketch, "E192.startSnap0", {"position": v(-67.17, 57.15) * mm});
            skLineSegment(sketch, "E193.MirrorCS", {"start": v(9.36, 15.88) * mm, "end": v(9.36, 51.65) * mm});
            skLineSegment(sketch, "E194.MirrorCS", {"start": v(9.36, 51.65) * mm, "end": v(6.19, 57.15) * mm});
            skLineSegment(sketch, "E195.MirrorCS", {"start": v(3.01, 51.65) * mm, "end": v(3.01, 15.87) * mm});
            skLineSegment(sketch, "E196", {"start": v(6.19, 57.15) * mm, "end": v(3.01, 51.65) * mm});
            skLineSegment(sketch, "E197", {"start": v(3.01, 12.7) * mm, "end": v(3.01, 15.88) * mm});
            skLineSegment(sketch, "E198", {"start": v(9.36, 15.88) * mm, "end": v(9.36, 12.7) * mm});
            skLineSegment(sketch, "E199", {"start": v(9.36, 12.7) * mm, "end": v(3.01, 12.7) * mm});
            skLineSegment(sketch, "E200", {"start": v(6.19, 57.15) * mm, "end": v(31.8, 57.15) * mm});
            skLineSegment(sketch, "E201", {"start": v(34.64, 60.37) * mm, "end": v(8.03, 60.37) * mm});
            skLineSegment(sketch, "E202", {"start": v(6.19, 57.15) * mm, "end": v(8.03, 60.37) * mm});
            skLineSegment(sketch, "E203", {"start": v(9.36, 51.65) * mm, "end": v(9.36, 57.15) * mm});
            skLineSegment(sketch, "E204", {"start": v(3.01, 51.65) * mm, "end": v(-8.5, 31.75) * mm});
            skLineSegment(sketch, "E205", {"start": v(-64.65, 57.15) * mm, "end": v(-64.65, 60.33) * mm, "construction": true});
            skLineSegment(sketch, "E206", {"start": v(6.19, 57.15) * mm, "end": v(2.46, 57.15) * mm, "construction": true});
            skLineSegment(sketch, "E207", {"start": v(4.33, 57.15) * mm, "end": v(4.33, 60.37) * mm, "construction": true});
            skLineSegment(sketch, "E208", {"start": v(-81.92, 60.33) * mm, "end": v(-78.67, 57.15) * mm});
            skLineSegment(sketch, "E209", {"start": v(34.67, 60.4) * mm, "end": v(31.8, 57.15) * mm});
            skLineSegment(sketch, "E210", {"start": v(3.01, 51.65) * mm, "end": v(9.36, 51.65) * mm, "construction": true});
            skSolve(sketch);
        }
        {
            var Q0;
            Q0=qCreatedBy(makeId("Front.planeOp"),FACE);
            var sketch = newSketch(context, id + "F4", { "sketchPlane" : qUnion([Q0])});
            skLineSegment(sketch, "E211.0", {"start": v(-50.7, 60.37) * mm, "end": v(4.33, 60.37) * mm});
            skLineSegment(sketch, "E212.0", {"start": v(-48.83, 57.15) * mm, "end": v(2.46, 57.15) * mm});
            skLineSegment(sketch, "E213", {"start": v(4.33, 60.37) * mm, "end": v(2.46, 57.15) * mm});
            skLineSegment(sketch, "E214", {"start": v(-50.7, 60.37) * mm, "end": v(-48.83, 57.15) * mm});
            skSolve(sketch);
        }
        {
            var Q0;
            Q0 = qSketchRegion(id + "F0", true);
            extrude(context, id + "F5", {"entities" : qUnion([Q0]), "endBound" : BoundingType.SYMMETRIC, "depth" : 38.1 * mm, "offsetDistance" : 25.4 * mm});
        }
        {
            var Q0;
            Q0 = qSketchRegion(id + "F1", true);
            var Q1;
            Q1 = qSketchRegion(id + "F2", true);
            extrude(context, id + "F6", {"entities" : qUnion([Q0, Q1]), "operationType" : NewBodyOperationType.ADD, "endBound" : BoundingType.SYMMETRIC, "depth" : 38.1 * mm, "offsetDistance" : 25.4 * mm});
        }
        {
            var Q0;
            Q0 = qSketchRegion(id + "F4", true);
            var Q1;
            Q1 = qSketchRegion(id + "F3", true);
            extrude(context, id + "F7", {"entities" : qUnion([Q0, Q1]), "operationType" : NewBodyOperationType.ADD, "endBound" : BoundingType.SYMMETRIC, "depth" : 38.1 * mm, "offsetDistance" : 25.4 * mm});
        }
        {
            var Q0;
            Q0=qCreatedBy(makeId("Right.planeOp"),FACE);
            var sketch = newSketch(context, id + "F8", { "sketchPlane" : qUnion([Q0])});
            skLineSegment(sketch, "E215", {"start": v(12.7, 12.7) * mm, "end": v(-12.7, 12.7) * mm});
            skLineSegment(sketch, "E216", {"start": v(-12.7, 12.7) * mm, "end": v(-12.7, 55.25) * mm});
            skLineSegment(sketch, "E217", {"start": v(-12.7, 55.25) * mm, "end": v(12.7, 55.25) * mm});
            skLineSegment(sketch, "E218", {"start": v(12.7, 55.25) * mm, "end": v(12.7, 12.7) * mm});
            skLineSegment(sketch, "E219", {"start": v(19.05, 12.7) * mm, "end": v(12.7, 12.7) * mm, "construction": true});
            skLineSegment(sketch, "E220", {"start": v(12.7, 60.33) * mm, "end": v(12.7, 55.25) * mm, "construction": true});
            skSolve(sketch);
        }
        {
            var Q0;
            Q0 = qSketchRegion(id + "F8", true);
            extrude(context, id + "F9", {"entities" : qUnion([Q0]), "operationType" : NewBodyOperationType.REMOVE, "endBound" : BoundingType.SYMMETRIC, "oppositeDirection" : true, "depth" : 2540 * mm, "offsetDistance" : 25.4 * mm});
        }
        {
            var Q0;
            Q0=qCreatedBy(makeId("Front.planeOp"),FACE);
            var sketch = newSketch(context, id + "F10", { "sketchPlane" : qUnion([Q0])});
            skLineSegment(sketch, "E221", {"start": v(-111.17, 6.35) * mm, "end": v(66.63, 6.35) * mm});
            skLineSegment(sketch, "E222", {"start": v(-111.17, 6.35) * mm, "end": v(-111.17, 0) * mm});
            skLineSegment(sketch, "E223", {"start": v(-111.17, 0) * mm, "end": v(66.63, 0) * mm});
            skLineSegment(sketch, "E224", {"start": v(66.63, 0) * mm, "end": v(66.63, 6.35) * mm});
            skSolve(sketch);
        }
        {
            var Q0;
            Q0 = qSketchRegion(id + "F10", true);
            extrude(context, id + "F11", {"entities" : qUnion([Q0]), "operationType" : NewBodyOperationType.REMOVE, "endBound" : BoundingType.SYMMETRIC, "oppositeDirection" : true, "depth" : 40.64 * mm, "offsetDistance" : 25.4 * mm});
        }
        {
            var Q0;
            Q0=qCreatedBy(makeId("Front.planeOp"),FACE);
            var sketch = newSketch(context, id + "F12", { "sketchPlane" : qUnion([Q0])});
            skLineSegment(sketch, "E225", {"start": v(66.63, 6.35) * mm, "end": v(66.63, -1.18) * mm, "construction": true});
            skLineSegment(sketch, "E226", {"start": v(66.63, -1.18) * mm, "end": v(41.23, -1.18) * mm, "construction": true});
            skLineSegment(sketch, "E227.1", {"start": v(-53.28, -41.36) * mm, "end": v(-81.42, 6.35) * mm});
            skLineSegment(sketch, "E228.1", {"start": v(-51.51, -37.99) * mm, "end": v(-75.93, 3.17) * mm});
            skLineSegment(sketch, "E229.0", {"start": v(45.58, 6.35) * mm, "end": v(18.01, -41.36) * mm});
            skPoint(sketch, "E229.0.midPoint", {"position": v(31.8, -17.5) * mm});
            skLineSegment(sketch, "E230.1", {"start": v(16.25, -37.98) * mm, "end": v(40.08, 3.18) * mm});
            skLineSegment(sketch, "E231", {"start": v(16.25, -37.98) * mm, "end": v(18.01, -41.36) * mm});
            skLineSegment(sketch, "E232", {"start": v(16.25, -37.98) * mm, "end": v(-51.51, -37.99) * mm});
            skLineSegment(sketch, "E233", {"start": v(-53.28, -41.36) * mm, "end": v(18.01, -41.36) * mm});
            skLineSegment(sketch, "E234", {"start": v(40.08, 6.35) * mm, "end": v(40.08, 3.18) * mm, "construction": true});
            skLineSegment(sketch, "E235", {"start": v(40.08, 3.18) * mm, "end": v(45.58, 6.35) * mm, "construction": true});
            skLineSegment(sketch, "E236", {"start": v(-75.93, 3.17) * mm, "end": v(-81.42, 6.35) * mm, "construction": true});
            skLineSegment(sketch, "E237", {"start": v(-51.51, -37.99) * mm, "end": v(-53.28, -41.36) * mm});
            skLineSegment(sketch, "E238", {"start": v(18.01, -41.36) * mm, "end": v(18.01, -34.94) * mm, "construction": true});
            skLineSegment(sketch, "E239", {"start": v(-53.28, -41.36) * mm, "end": v(-53.28, -35.01) * mm, "construction": true});
            skLineSegment(sketch, "E240", {"start": v(-75.93, 3.17) * mm, "end": v(-75.93, 6.35) * mm, "construction": true});
            skLineSegment(sketch, "E241", {"start": v(-81.42, 6.35) * mm, "end": v(45.58, 6.35) * mm});
            skLineSegment(sketch, "E242", {"start": v(40.08, 3.18) * mm, "end": v(-75.93, 3.17) * mm});
            skLineSegment(sketch, "E243", {"start": v(40.08, 3.18) * mm, "end": v(40.08, 6.35) * mm, "construction": true});
            skLineSegment(sketch, "E244", {"start": v(-46.7, -41.36) * mm, "end": v(-46.7, -37.99) * mm, "construction": true});
            skLineSegment(sketch, "E245", {"start": v(9.41, -41.36) * mm, "end": v(9.41, -37.98) * mm, "construction": true});
            skSolve(sketch);
        }
        {
            var Q0;
            Q0=qCreatedBy(makeId("Front.planeOp"),FACE);
            var sketch = newSketch(context, id + "F13", { "sketchPlane" : qUnion([Q0])});
            skLineSegment(sketch, "E246", {"start": v(-51.51, -37.99) * mm, "end": v(-51.51, 3.17) * mm, "construction": true});
            skLineSegment(sketch, "E247.0", {"start": v(-37.96, 3.17) * mm, "end": v(-44.74, -37.99) * mm, "construction": true});
            skLineSegment(sketch, "E247.1", {"start": v(-44.74, -37.99) * mm, "end": v(-51.51, 3.17) * mm, "construction": true});
            skLineSegment(sketch, "E247.2", {"start": v(-51.51, 3.17) * mm, "end": v(-37.96, 3.17) * mm, "construction": true});
            skLineSegment(sketch, "E248", {"start": v(-44.74, 3.17) * mm, "end": v(-44.74, -37.99) * mm, "construction": true});
            skLineSegment(sketch, "E249", {"start": v(-44.74, -37.99) * mm, "end": v(-51.51, -37.99) * mm, "construction": true});
            skLineSegment(sketch, "E250.0", {"start": v(-44.74, -37.99) * mm, "end": v(-37.96, 3.17) * mm, "construction": true});
            skLineSegment(sketch, "E250.2", {"start": v(-31.18, -37.99) * mm, "end": v(-44.74, -37.99) * mm, "construction": true});
            skLineSegment(sketch, "E251.direction1", {"start": v(-44.74, -37.99) * mm, "end": v(-31.18, -37.99) * mm, "construction": true});
            skLineSegment(sketch, "E252", {"start": v(-37.96, 3.17) * mm, "end": v(-31.18, -37.99) * mm, "construction": true});
            skLineSegment(sketch, "E253.0", {"start": v(-24.4, 3.17) * mm, "end": v(-31.18, -37.99) * mm, "construction": true});
            skLineSegment(sketch, "E253.1", {"start": v(-31.18, -37.99) * mm, "end": v(-37.96, 3.17) * mm, "construction": true});
            skLineSegment(sketch, "E253.2", {"start": v(-37.96, 3.17) * mm, "end": v(-24.4, 3.17) * mm, "construction": true});
            skLineSegment(sketch, "E254.2", {"start": v(-17.63, -37.98) * mm, "end": v(-31.18, -37.99) * mm, "construction": true});
            skLineSegment(sketch, "E255.1", {"start": v(-17.63, -37.98) * mm, "end": v(-24.4, 3.17) * mm, "construction": true});
            skLineSegment(sketch, "E256.2", {"start": v(-24.4, 3.17) * mm, "end": v(-10.86, 3.17) * mm, "construction": true});
            skLineSegment(sketch, "E257.0", {"start": v(-10.86, 3.17) * mm, "end": v(-17.63, -37.98) * mm, "construction": true});
            skLineSegment(sketch, "E258.2", {"start": v(-4.08, -37.98) * mm, "end": v(-17.63, -37.98) * mm, "construction": true});
            skLineSegment(sketch, "E259.1", {"start": v(-4.08, -37.98) * mm, "end": v(-10.86, 3.17) * mm, "construction": true});
            skLineSegment(sketch, "E260.2", {"start": v(-10.86, 3.17) * mm, "end": v(2.7, 3.17) * mm, "construction": true});
            skLineSegment(sketch, "E261.0", {"start": v(2.7, 3.17) * mm, "end": v(-4.08, -37.98) * mm, "construction": true});
            skLineSegment(sketch, "E262.2", {"start": v(9.47, -37.99) * mm, "end": v(-4.08, -37.99) * mm, "construction": true});
            skLineSegment(sketch, "E263.1", {"start": v(9.47, -37.99) * mm, "end": v(2.7, 3.17) * mm, "construction": true});
            skLineSegment(sketch, "E264.2", {"start": v(2.7, 3.17) * mm, "end": v(16.25, 3.17) * mm, "construction": true});
            skLineSegment(sketch, "E265.0", {"start": v(16.25, 3.17) * mm, "end": v(9.47, -37.98) * mm, "construction": true});
            skLineSegment(sketch, "E266", {"start": v(16.25, 3.17) * mm, "end": v(16.25, -37.98) * mm, "construction": true});
            skLineSegment(sketch, "E267", {"start": v(16.25, -37.98) * mm, "end": v(9.47, -37.98) * mm, "construction": true});
            skLineSegment(sketch, "E268", {"start": v(-51.51, -17.4) * mm, "end": v(16.25, -17.4) * mm, "construction": true});
            skLineSegment(sketch, "E269.MirrorCS", {"start": v(-37.96, -37.99) * mm, "end": v(-31.18, 3.17) * mm, "construction": true});
            skLineSegment(sketch, "E270.MirrorCS", {"start": v(2.7, -37.99) * mm, "end": v(-4.08, 3.17) * mm, "construction": true});
            skLineSegment(sketch, "E271.MirrorCS", {"start": v(-44.74, 3.17) * mm, "end": v(-31.18, 3.17) * mm, "construction": true});
            skLineSegment(sketch, "E272.MirrorCS", {"start": v(-10.86, -37.99) * mm, "end": v(-17.63, 3.17) * mm, "construction": true});
            skLineSegment(sketch, "E273.MirrorCS", {"start": v(-24.4, -37.99) * mm, "end": v(-31.18, 3.17) * mm, "construction": true});
            skLineSegment(sketch, "E274.MirrorCS", {"start": v(-4.08, 3.17) * mm, "end": v(-10.86, -37.99) * mm, "construction": true});
            skLineSegment(sketch, "E275.MirrorCS", {"start": v(-37.96, -37.99) * mm, "end": v(-44.74, 3.17) * mm, "construction": true});
            skLineSegment(sketch, "E276.MirrorCS", {"start": v(-17.63, 3.17) * mm, "end": v(-24.4, -37.99) * mm, "construction": true});
            skLineSegment(sketch, "E277.MirrorCS", {"start": v(9.47, 3.17) * mm, "end": v(2.7, -37.98) * mm, "construction": true});
            skLineSegment(sketch, "E278.MirrorCS", {"start": v(2.7, -37.98) * mm, "end": v(16.25, -37.98) * mm, "construction": true});
            skLineSegment(sketch, "E279.MirrorCS", {"start": v(-24.4, -37.99) * mm, "end": v(-10.86, -37.99) * mm, "construction": true});
            skLineSegment(sketch, "E280.MirrorCS", {"start": v(-31.18, 3.17) * mm, "end": v(-44.74, 3.17) * mm, "construction": true});
            skLineSegment(sketch, "E281.MirrorCS", {"start": v(-4.08, 3.17) * mm, "end": v(-17.63, 3.17) * mm, "construction": true});
            skLineSegment(sketch, "E282.MirrorCS", {"start": v(-10.86, -37.99) * mm, "end": v(2.7, -37.99) * mm, "construction": true});
            skLineSegment(sketch, "E283.MirrorCS", {"start": v(9.47, 3.17) * mm, "end": v(-4.08, 3.17) * mm, "construction": true});
            skLineSegment(sketch, "E284.MirrorCS", {"start": v(-17.63, 3.17) * mm, "end": v(-31.18, 3.17) * mm, "construction": true});
            skLineSegment(sketch, "E285.MirrorCS", {"start": v(-44.74, -37.99) * mm, "end": v(-44.74, 3.17) * mm, "construction": true});
            skLineSegment(sketch, "E286.MirrorCS", {"start": v(-44.74, 3.17) * mm, "end": v(-51.51, 3.17) * mm, "construction": true});
            skLineSegment(sketch, "E287.MirrorCS", {"start": v(-44.74, 3.17) * mm, "end": v(-51.51, -37.99) * mm, "construction": true});
            skLineSegment(sketch, "E288.MirrorCS", {"start": v(-44.74, 3.17) * mm, "end": v(-37.96, -37.99) * mm, "construction": true});
            skLineSegment(sketch, "E289.MirrorCS", {"start": v(16.25, 3.17) * mm, "end": v(9.47, 3.17) * mm, "construction": true});
            skLineSegment(sketch, "E290.MirrorCS", {"start": v(-51.51, 3.17) * mm, "end": v(-51.51, -37.99) * mm, "construction": true});
            skLineSegment(sketch, "E291.MirrorCS", {"start": v(-37.96, -37.99) * mm, "end": v(-24.4, -37.99) * mm, "construction": true});
            skLineSegment(sketch, "E292.MirrorCS", {"start": v(16.25, -37.98) * mm, "end": v(16.25, 3.17) * mm, "construction": true});
            skLineSegment(sketch, "E293.MirrorCS", {"start": v(-51.51, -37.99) * mm, "end": v(-37.96, -37.99) * mm, "construction": true});
            skLineSegment(sketch, "E294.MirrorCS", {"start": v(16.25, -37.99) * mm, "end": v(9.47, 3.17) * mm, "construction": true});
            skLineSegment(sketch, "E295.MirrorCS", {"start": v(-31.18, 3.17) * mm, "end": v(-37.96, -37.99) * mm, "construction": true});
            skSolve(sketch);
        }
        {
            var Q0;
            Q0 = qSketchRegion(id + "F12", true);
            extrude(context, id + "F14", {"entities" : qUnion([Q0]), "operationType" : NewBodyOperationType.ADD, "endBound" : BoundingType.SYMMETRIC, "depth" : 38.1 * mm, "offsetDistance" : 25.4 * mm});
        }
        {
            var Q0;
            Q0=qCreatedBy(makeId("Front.planeOp"),FACE);
            var sketch = newSketch(context, id + "F15", { "sketchPlane" : qUnion([Q0])});
            skLineSegment(sketch, "E296.0", {"start": v(-44.74, -37.99) * mm, "end": v(-51.51, 3.17) * mm, "construction": true});
            skLineSegment(sketch, "E297.0", {"start": v(-44.74, -37.99) * mm, "end": v(-37.96, 3.17) * mm, "construction": true});
            skLineSegment(sketch, "E298.0", {"start": v(-31.18, -37.99) * mm, "end": v(-37.96, 3.17) * mm, "construction": true});
            skLineSegment(sketch, "E299.0", {"start": v(-24.4, 3.17) * mm, "end": v(-31.18, -37.99) * mm, "construction": true});
            skLineSegment(sketch, "E300.0", {"start": v(-17.63, -37.98) * mm, "end": v(-24.4, 3.17) * mm, "construction": true});
            skLineSegment(sketch, "E301.0", {"start": v(-10.86, 3.17) * mm, "end": v(-17.63, -37.98) * mm, "construction": true});
            skLineSegment(sketch, "E302.0", {"start": v(-4.08, -37.98) * mm, "end": v(-10.86, 3.17) * mm, "construction": true});
            skLineSegment(sketch, "E303.0", {"start": v(2.7, 3.17) * mm, "end": v(-4.08, -37.98) * mm, "construction": true});
            skLineSegment(sketch, "E304.0", {"start": v(9.47, -37.99) * mm, "end": v(2.7, 3.17) * mm, "construction": true});
            skLineSegment(sketch, "E305.0", {"start": v(16.25, 3.17) * mm, "end": v(9.47, -37.98) * mm, "construction": true});
            skLineSegment(sketch, "E306", {"start": v(-44.74, 3.17) * mm, "end": v(-44.74, -28.4) * mm, "construction": true});
            skLineSegment(sketch, "E307", {"start": v(-44.74, -37.99) * mm, "end": v(-44.74, -31.64) * mm});
            skLineSegment(sketch, "E308", {"start": v(-44.74, -31.64) * mm, "end": v(-45.78, -31.63) * mm, "construction": true});
            skLineSegment(sketch, "E309", {"start": v(-51.51, 3.17) * mm, "end": v(-50.47, 3.17) * mm});
            skLineSegment(sketch, "E310", {"start": v(-50.47, 3.17) * mm, "end": v(-44.74, -31.64) * mm});
            skLineSegment(sketch, "E311", {"start": v(-37.96, 3.17) * mm, "end": v(-39, 3.17) * mm});
            skLineSegment(sketch, "E312", {"start": v(-44.74, -31.64) * mm, "end": v(-39, 3.17) * mm});
            skLineSegment(sketch, "E313", {"start": v(-37.96, 3.17) * mm, "end": v(-37.96, -3.18) * mm});
            skLineSegment(sketch, "E314", {"start": v(-37.96, -3.18) * mm, "end": v(-43.7, -37.99) * mm});
            skLineSegment(sketch, "E315", {"start": v(-43.7, -37.99) * mm, "end": v(-44.74, -37.99) * mm});
            skLineSegment(sketch, "E316.MirrorCS", {"start": v(-51.51, -3.18) * mm, "end": v(-45.78, -37.99) * mm});
            skLineSegment(sketch, "E317.MirrorCS", {"start": v(-51.51, 3.17) * mm, "end": v(-51.51, -3.18) * mm});
            skLineSegment(sketch, "E318.MirrorCS", {"start": v(-45.78, -37.99) * mm, "end": v(-44.74, -37.99) * mm});
            skLineSegment(sketch, "E319.MirrorCS", {"start": v(-31.19, -31.64) * mm, "end": v(-36.92, 3.17) * mm});
            skLineSegment(sketch, "E320.MirrorCS", {"start": v(-37.96, 3.17) * mm, "end": v(-36.92, 3.17) * mm});
            skLineSegment(sketch, "E321.MirrorCS", {"start": v(-32.23, -37.99) * mm, "end": v(-31.19, -37.99) * mm});
            skLineSegment(sketch, "E322.MirrorCS", {"start": v(-37.96, -3.18) * mm, "end": v(-32.23, -37.99) * mm});
            skLineSegment(sketch, "E323.MirrorCS", {"start": v(-31.19, -37.99) * mm, "end": v(-31.19, -31.64) * mm});
            skLineSegment(sketch, "E324.MirrorCS", {"start": v(-31.19, -31.64) * mm, "end": v(-25.45, 3.17) * mm});
            skLineSegment(sketch, "E325.MirrorCS", {"start": v(-24.4, -3.18) * mm, "end": v(-30.14, -37.99) * mm});
            skLineSegment(sketch, "E326.MirrorCS", {"start": v(-30.14, -37.99) * mm, "end": v(-31.19, -37.99) * mm});
            skLineSegment(sketch, "E327.MirrorCS", {"start": v(-24.4, 3.17) * mm, "end": v(-25.45, 3.17) * mm});
            skLineSegment(sketch, "E328.MirrorCS", {"start": v(-24.4, 3.17) * mm, "end": v(-24.4, -3.18) * mm});
            skLineSegment(sketch, "E329.MirrorCS", {"start": v(-17.64, -31.64) * mm, "end": v(-23.36, 3.17) * mm});
            skLineSegment(sketch, "E330.MirrorCS", {"start": v(-24.4, -3.18) * mm, "end": v(-18.68, -37.99) * mm});
            skLineSegment(sketch, "E331.MirrorCS", {"start": v(-17.64, -37.99) * mm, "end": v(-17.64, -31.64) * mm});
            skLineSegment(sketch, "E332.MirrorCS", {"start": v(-18.68, -37.99) * mm, "end": v(-17.64, -37.99) * mm});
            skLineSegment(sketch, "E333.MirrorCS", {"start": v(-24.4, 3.17) * mm, "end": v(-23.36, 3.17) * mm});
            skLineSegment(sketch, "E334.MirrorCS", {"start": v(-17.64, -31.64) * mm, "end": v(-11.9, 3.17) * mm});
            skLineSegment(sketch, "E335.MirrorCS", {"start": v(-10.85, -3.18) * mm, "end": v(-16.6, -37.99) * mm});
            skLineSegment(sketch, "E336.MirrorCS", {"start": v(-16.6, -37.99) * mm, "end": v(-17.64, -37.99) * mm});
            skLineSegment(sketch, "E337.MirrorCS", {"start": v(-10.85, 3.17) * mm, "end": v(-11.9, 3.17) * mm});
            skLineSegment(sketch, "E338.MirrorCS", {"start": v(-10.85, 3.17) * mm, "end": v(-10.85, -3.18) * mm});
            skLineSegment(sketch, "E339.MirrorCS", {"start": v(-10.85, 3.17) * mm, "end": v(-9.8, 3.17) * mm});
            skLineSegment(sketch, "E340.MirrorCS", {"start": v(-4.09, -31.64) * mm, "end": v(-9.8, 3.17) * mm});
            skLineSegment(sketch, "E341.MirrorCS", {"start": v(-10.85, -3.18) * mm, "end": v(-5.13, -38) * mm});
            skLineSegment(sketch, "E342.MirrorCS", {"start": v(-4.09, -38) * mm, "end": v(-4.09, -31.64) * mm});
            skLineSegment(sketch, "E343.MirrorCS", {"start": v(-5.13, -38) * mm, "end": v(-4.09, -38) * mm});
            skLineSegment(sketch, "E344.MirrorCS", {"start": v(-4.09, -31.64) * mm, "end": v(1.66, 3.16) * mm});
            skLineSegment(sketch, "E345.MirrorCS", {"start": v(2.7, -3.19) * mm, "end": v(-3.04, -38) * mm});
            skLineSegment(sketch, "E346.MirrorCS", {"start": v(-3.04, -38) * mm, "end": v(-4.09, -38) * mm});
            skLineSegment(sketch, "E347.MirrorCS", {"start": v(2.7, 3.16) * mm, "end": v(1.66, 3.16) * mm});
            skLineSegment(sketch, "E348.MirrorCS", {"start": v(2.7, 3.16) * mm, "end": v(2.7, -3.19) * mm});
            skLineSegment(sketch, "E349.MirrorCS", {"start": v(2.7, 3.16) * mm, "end": v(3.75, 3.16) * mm});
            skLineSegment(sketch, "E350.MirrorCS", {"start": v(9.46, -31.65) * mm, "end": v(3.75, 3.16) * mm});
            skLineSegment(sketch, "E351.MirrorCS", {"start": v(2.7, -3.19) * mm, "end": v(8.42, -38) * mm});
            skLineSegment(sketch, "E352.MirrorCS", {"start": v(9.46, -38) * mm, "end": v(9.46, -31.65) * mm});
            skLineSegment(sketch, "E353.MirrorCS", {"start": v(8.42, -38) * mm, "end": v(9.46, -38) * mm});
            skLineSegment(sketch, "E354.MirrorCS", {"start": v(9.46, -31.65) * mm, "end": v(15.22, 3.16) * mm});
            skLineSegment(sketch, "E355.MirrorCS", {"start": v(16.26, -3.2) * mm, "end": v(10.5, -38) * mm});
            skLineSegment(sketch, "E356.MirrorCS", {"start": v(10.5, -38) * mm, "end": v(9.46, -38) * mm});
            skLineSegment(sketch, "E357.MirrorCS", {"start": v(16.26, 3.15) * mm, "end": v(15.22, 3.16) * mm});
            skLineSegment(sketch, "E358.MirrorCS", {"start": v(16.26, 3.15) * mm, "end": v(16.26, -3.2) * mm});
            skLineSegment(sketch, "E359", {"start": v(15.85, -5.66) * mm, "end": v(13.82, -5.33) * mm, "construction": true});
            skLineSegment(sketch, "E360", {"start": v(16.26, -3.2) * mm, "end": v(16.25, -37.99) * mm});
            skLineSegment(sketch, "E361", {"start": v(16.26, -9.45) * mm, "end": v(15.23, -9.45) * mm, "construction": true});
            skLineSegment(sketch, "E362", {"start": v(15.23, -9.45) * mm, "end": v(15.22, -37.98) * mm});
            skLineSegment(sketch, "E363", {"start": v(15.22, -37.98) * mm, "end": v(16.25, -37.99) * mm});
            skLineSegment(sketch, "E364", {"start": v(-51.51, -3.18) * mm, "end": v(-51.51, -37.99) * mm});
            skLineSegment(sketch, "E365", {"start": v(-51.51, -9.44) * mm, "end": v(-50.48, -9.44) * mm, "construction": true});
            skLineSegment(sketch, "E366", {"start": v(-50.48, -9.44) * mm, "end": v(-50.48, -37.99) * mm});
            skLineSegment(sketch, "E367", {"start": v(-50.48, -37.99) * mm, "end": v(-51.51, -37.99) * mm});
            skLineSegment(sketch, "E368.MirrorCS", {"start": v(-30.14, 3.17) * mm, "end": v(-31.19, 3.17) * mm});
            skLineSegment(sketch, "E369.MirrorCS", {"start": v(-10.85, -37.98) * mm, "end": v(-9.8, -37.98) * mm});
            skLineSegment(sketch, "E370.MirrorCS", {"start": v(-37.96, -37.99) * mm, "end": v(-36.92, -37.99) * mm});
            skLineSegment(sketch, "E371.MirrorCS", {"start": v(-45.78, 3.17) * mm, "end": v(-44.74, 3.17) * mm});
            skLineSegment(sketch, "E372.MirrorCS", {"start": v(-24.4, -37.99) * mm, "end": v(-23.36, -37.99) * mm});
            skLineSegment(sketch, "E373.MirrorCS", {"start": v(-3.04, 3.18) * mm, "end": v(-4.09, 3.18) * mm});
            skLineSegment(sketch, "E374.MirrorCS", {"start": v(-16.6, 3.17) * mm, "end": v(-17.64, 3.17) * mm});
            skLineSegment(sketch, "E375.MirrorCS", {"start": v(10.5, 3.18) * mm, "end": v(9.46, 3.18) * mm});
            skLineSegment(sketch, "E376.MirrorCS", {"start": v(-44.74, -3.18) * mm, "end": v(-45.78, -3.18) * mm, "construction": true});
            skLineSegment(sketch, "E377.MirrorCS", {"start": v(-51.51, -37.99) * mm, "end": v(-50.47, -37.99) * mm});
            skLineSegment(sketch, "E378.MirrorCS", {"start": v(16.26, -25.37) * mm, "end": v(15.23, -25.37) * mm, "construction": true});
            skLineSegment(sketch, "E379.MirrorCS", {"start": v(-43.7, 3.17) * mm, "end": v(-44.74, 3.17) * mm});
            skLineSegment(sketch, "E380.MirrorCS", {"start": v(-10.85, -37.98) * mm, "end": v(-11.9, -37.98) * mm});
            skLineSegment(sketch, "E381.MirrorCS", {"start": v(16.26, -37.97) * mm, "end": v(15.22, -37.97) * mm});
            skLineSegment(sketch, "E382.MirrorCS", {"start": v(-5.13, 3.18) * mm, "end": v(-4.09, 3.18) * mm});
            skLineSegment(sketch, "E383.MirrorCS", {"start": v(2.7, -37.98) * mm, "end": v(3.75, -37.98) * mm});
            skLineSegment(sketch, "E384.MirrorCS", {"start": v(8.42, 3.18) * mm, "end": v(9.46, 3.18) * mm});
            skLineSegment(sketch, "E385.MirrorCS", {"start": v(2.7, -37.98) * mm, "end": v(1.66, -37.98) * mm});
            skLineSegment(sketch, "E386.MirrorCS", {"start": v(-24.4, -37.99) * mm, "end": v(-25.45, -37.99) * mm});
            skLineSegment(sketch, "E387.MirrorCS", {"start": v(-37.96, -37.99) * mm, "end": v(-39, -37.99) * mm});
            skLineSegment(sketch, "E388.MirrorCS", {"start": v(15.22, 3.17) * mm, "end": v(16.25, 3.17) * mm});
            skLineSegment(sketch, "E389.MirrorCS", {"start": v(-32.23, 3.17) * mm, "end": v(-31.19, 3.17) * mm});
            skLineSegment(sketch, "E390.MirrorCS", {"start": v(-18.68, 3.17) * mm, "end": v(-17.64, 3.17) * mm});
            skLineSegment(sketch, "E391.MirrorCS", {"start": v(-50.48, 3.17) * mm, "end": v(-51.51, 3.17) * mm});
            skLineSegment(sketch, "E392.MirrorCS", {"start": v(-51.51, -25.37) * mm, "end": v(-50.48, -25.37) * mm, "construction": true});
            skLineSegment(sketch, "E393.MirrorCS", {"start": v(15.85, -29.15) * mm, "end": v(13.82, -29.49) * mm, "construction": true});
            skLineSegment(sketch, "E394.MirrorCS", {"start": v(-4.09, -3.17) * mm, "end": v(1.66, -37.98) * mm});
            skLineSegment(sketch, "E395.MirrorCS", {"start": v(-17.64, 3.17) * mm, "end": v(-17.64, -3.18) * mm});
            skLineSegment(sketch, "E396.MirrorCS", {"start": v(-50.47, -37.99) * mm, "end": v(-44.74, -3.18) * mm});
            skLineSegment(sketch, "E397.MirrorCS", {"start": v(-31.19, -3.18) * mm, "end": v(-36.92, -37.99) * mm});
            skLineSegment(sketch, "E398.MirrorCS", {"start": v(-10.85, -37.98) * mm, "end": v(-10.85, -31.63) * mm});
            skLineSegment(sketch, "E399.MirrorCS", {"start": v(-37.96, -31.64) * mm, "end": v(-32.23, 3.17) * mm});
            skLineSegment(sketch, "E400.MirrorCS", {"start": v(2.7, -37.98) * mm, "end": v(2.7, -31.63) * mm});
            skLineSegment(sketch, "E401.MirrorCS", {"start": v(-31.18, 3.17) * mm, "end": v(-37.96, -37.99) * mm, "construction": true});
            skLineSegment(sketch, "E402.MirrorCS", {"start": v(-4.09, -3.17) * mm, "end": v(-9.8, -37.98) * mm});
            skLineSegment(sketch, "E403.MirrorCS", {"start": v(-17.64, -3.18) * mm, "end": v(-11.9, -37.98) * mm});
            skLineSegment(sketch, "E404.MirrorCS", {"start": v(-24.4, -37.99) * mm, "end": v(-31.18, 3.17) * mm, "construction": true});
            skLineSegment(sketch, "E405.MirrorCS", {"start": v(-17.64, -3.18) * mm, "end": v(-23.36, -37.99) * mm});
            skLineSegment(sketch, "E406.MirrorCS", {"start": v(2.7, -31.63) * mm, "end": v(-3.04, 3.18) * mm});
            skLineSegment(sketch, "E407.MirrorCS", {"start": v(-51.51, -37.99) * mm, "end": v(-51.51, -31.64) * mm});
            skLineSegment(sketch, "E408.MirrorCS", {"start": v(-44.74, -37.99) * mm, "end": v(-44.74, -6.42) * mm, "construction": true});
            skLineSegment(sketch, "E409.MirrorCS", {"start": v(15.23, -25.37) * mm, "end": v(15.22, 3.17) * mm});
            skLineSegment(sketch, "E410.MirrorCS", {"start": v(-44.74, 3.17) * mm, "end": v(-37.96, -37.99) * mm, "construction": true});
            skLineSegment(sketch, "E411.MirrorCS", {"start": v(-4.08, 3.17) * mm, "end": v(-10.86, -37.99) * mm, "construction": true});
            skLineSegment(sketch, "E412.MirrorCS", {"start": v(-10.86, -37.99) * mm, "end": v(-17.63, 3.17) * mm, "construction": true});
            skLineSegment(sketch, "E413.MirrorCS", {"start": v(16.26, -31.62) * mm, "end": v(16.25, 3.17) * mm});
            skLineSegment(sketch, "E414.MirrorCS", {"start": v(-24.4, -31.64) * mm, "end": v(-30.14, 3.17) * mm});
            skLineSegment(sketch, "E415.MirrorCS", {"start": v(-37.96, -37.99) * mm, "end": v(-37.96, -31.64) * mm});
            skLineSegment(sketch, "E416.MirrorCS", {"start": v(-44.74, 3.17) * mm, "end": v(-51.51, -37.99) * mm, "construction": true});
            skLineSegment(sketch, "E417.MirrorCS", {"start": v(-10.85, -31.63) * mm, "end": v(-5.13, 3.18) * mm});
            skLineSegment(sketch, "E418.MirrorCS", {"start": v(-31.19, -3.18) * mm, "end": v(-25.45, -37.99) * mm});
            skLineSegment(sketch, "E419.MirrorCS", {"start": v(-4.09, 3.18) * mm, "end": v(-4.09, -3.17) * mm});
            skLineSegment(sketch, "E420.MirrorCS", {"start": v(-24.4, -31.64) * mm, "end": v(-18.68, 3.17) * mm});
            skLineSegment(sketch, "E421.MirrorCS", {"start": v(-10.85, -31.63) * mm, "end": v(-16.6, 3.17) * mm});
            skLineSegment(sketch, "E422.MirrorCS", {"start": v(-24.4, -37.99) * mm, "end": v(-24.4, -31.64) * mm});
            skLineSegment(sketch, "E423.MirrorCS", {"start": v(-44.74, -3.18) * mm, "end": v(-39, -37.99) * mm});
            skLineSegment(sketch, "E424.MirrorCS", {"start": v(-31.19, 3.17) * mm, "end": v(-31.19, -3.18) * mm});
            skLineSegment(sketch, "E425.MirrorCS", {"start": v(-44.74, 3.17) * mm, "end": v(-44.74, -3.18) * mm});
            skLineSegment(sketch, "E426.MirrorCS", {"start": v(2.7, -37.99) * mm, "end": v(-4.08, 3.17) * mm, "construction": true});
            skLineSegment(sketch, "E427.MirrorCS", {"start": v(-51.51, -31.64) * mm, "end": v(-45.78, 3.17) * mm});
            skLineSegment(sketch, "E428.MirrorCS", {"start": v(9.46, 3.18) * mm, "end": v(9.46, -3.17) * mm});
            skLineSegment(sketch, "E429.MirrorCS", {"start": v(9.46, -3.17) * mm, "end": v(15.22, -37.97) * mm});
            skLineSegment(sketch, "E430.MirrorCS", {"start": v(-17.63, 3.17) * mm, "end": v(-24.4, -37.99) * mm, "construction": true});
            skLineSegment(sketch, "E431.MirrorCS", {"start": v(-50.48, -25.37) * mm, "end": v(-50.48, 3.17) * mm});
            skLineSegment(sketch, "E432.MirrorCS", {"start": v(9.46, -3.17) * mm, "end": v(3.75, -37.98) * mm});
            skLineSegment(sketch, "E433.MirrorCS", {"start": v(16.26, -37.97) * mm, "end": v(16.26, -31.62) * mm});
            skLineSegment(sketch, "E434.MirrorCS", {"start": v(16.26, -31.62) * mm, "end": v(10.5, 3.18) * mm});
            skLineSegment(sketch, "E435.MirrorCS", {"start": v(9.47, 3.17) * mm, "end": v(2.7, -37.98) * mm, "construction": true});
            skLineSegment(sketch, "E436.MirrorCS", {"start": v(2.7, -31.63) * mm, "end": v(8.42, 3.18) * mm});
            skLineSegment(sketch, "E437.MirrorCS", {"start": v(-37.96, -31.64) * mm, "end": v(-43.7, 3.17) * mm});
            skLineSegment(sketch, "E438.MirrorCS", {"start": v(-51.51, -31.64) * mm, "end": v(-51.51, 3.17) * mm});
            skLineSegment(sketch, "E439.MirrorCS", {"start": v(16.25, -37.99) * mm, "end": v(9.47, 3.17) * mm, "construction": true});
            skSolve(sketch);
        }
        {
            var Q0;
            Q0=qCreatedBy(makeId("Front.planeOp"),FACE);
            var sketch = newSketch(context, id + "F16", { "sketchPlane" : qUnion([Q0])});
            skLineSegment(sketch, "E440.0.0", {"start": v(-57.58, -4.06) * mm, "end": v(-51.51, 3.17) * mm});
            skLineSegment(sketch, "E440.0.1", {"start": v(-51.51, 3.17) * mm, "end": v(-51.51, 3.17) * mm});
            skLineSegment(sketch, "E440.0.2", {"start": v(-51.51, 3.17) * mm, "end": v(-51.51, 3.17) * mm});
            skLineSegment(sketch, "E440.0.3", {"start": v(-51.51, 3.17) * mm, "end": v(-51.51, 3.17) * mm});
            skLineSegment(sketch, "E440.0.4", {"start": v(-51.51, 3.17) * mm, "end": v(-54.69, 3.17) * mm});
            skLineSegment(sketch, "E440.0.5", {"start": v(-54.69, 3.17) * mm, "end": v(-67.14, -11.65) * mm});
            skLineSegment(sketch, "E440.0.6", {"start": v(-67.14, -11.65) * mm, "end": v(-65.82, -13.86) * mm});
            skLineSegment(sketch, "E440.0.7", {"start": v(-65.82, -13.86) * mm, "end": v(-59.75, -6.63) * mm});
            skLineSegment(sketch, "E440.0.8", {"start": v(-59.75, -6.63) * mm, "end": v(-57.58, -4.06) * mm});
            skLineSegment(sketch, "E441.0.0", {"start": v(-51.51, -20.52) * mm, "end": v(-51.51, -17.4) * mm});
            skLineSegment(sketch, "E441.0.1", {"start": v(-51.51, -17.4) * mm, "end": v(-51.51, -14.3) * mm});
            skLineSegment(sketch, "E441.0.2", {"start": v(-51.51, -14.3) * mm, "end": v(-57.58, -4.06) * mm});
            skLineSegment(sketch, "E441.0.3", {"start": v(-57.58, -4.06) * mm, "end": v(-59.75, -6.63) * mm});
            skLineSegment(sketch, "E441.0.4", {"start": v(-59.75, -6.63) * mm, "end": v(-51.51, -20.52) * mm});
            skLineSegment(sketch, "E442.MirrorCS", {"start": v(16.27, 3.14) * mm, "end": v(16.27, 3.15) * mm});
            skLineSegment(sketch, "E443.MirrorCS", {"start": v(16.27, 3.15) * mm, "end": v(16.26, 3.15) * mm});
            skLineSegment(sketch, "E444.MirrorCS", {"start": v(16.26, 3.15) * mm, "end": v(16.25, 3.17) * mm});
            skLineSegment(sketch, "E445.MirrorCS", {"start": v(31.6, -11.47) * mm, "end": v(30.3, -13.71) * mm});
            skLineSegment(sketch, "E446.MirrorCS", {"start": v(24.48, -6.48) * mm, "end": v(22.32, -3.9) * mm});
            skLineSegment(sketch, "E447.MirrorCS", {"start": v(16.25, -17.26) * mm, "end": v(16.25, -14.15) * mm});
            skLineSegment(sketch, "E448.MirrorCS", {"start": v(30.3, -13.71) * mm, "end": v(24.48, -6.48) * mm});
            skLineSegment(sketch, "E449.MirrorCS", {"start": v(24.48, -6.48) * mm, "end": v(16.25, -20.37) * mm});
            skLineSegment(sketch, "E450.MirrorCS", {"start": v(22.32, -3.9) * mm, "end": v(16.27, 3.14) * mm});
            skLineSegment(sketch, "E451.MirrorCS", {"start": v(22.32, -3.9) * mm, "end": v(24.48, -6.48) * mm});
            skLineSegment(sketch, "E452.MirrorCS", {"start": v(19.42, 3.17) * mm, "end": v(31.6, -11.47) * mm});
            skLineSegment(sketch, "E453.MirrorCS", {"start": v(16.25, -20.37) * mm, "end": v(16.25, -17.26) * mm});
            skLineSegment(sketch, "E454.MirrorCS", {"start": v(16.25, 3.17) * mm, "end": v(19.42, 3.17) * mm});
            skLineSegment(sketch, "E455.MirrorCS", {"start": v(16.25, -14.15) * mm, "end": v(22.32, -3.9) * mm});
            skSolve(sketch);
        }
        {
            var Q0;
            Q0 = qSketchRegion(id + "F16", true);
            extrude(context, id + "F17", {"entities" : qUnion([Q0]), "operationType" : NewBodyOperationType.ADD, "endBound" : BoundingType.SYMMETRIC, "depth" : 38.1 * mm, "offsetDistance" : 25.4 * mm});
        }
        {
            var Q0;
            Q0 = qSketchRegion(id + "F15", true);
            extrude(context, id + "F18", {"entities" : qUnion([Q0]), "endBound" : BoundingType.SYMMETRIC, "depth" : 38.1 * mm, "offsetDistance" : 25.4 * mm});
        }
        {
            var Q0;
            Q0=qCreatedBy(makeId("Right.planeOp"),FACE);
            var sketch = newSketch(context, id + "F19", { "sketchPlane" : qUnion([Q0])});
            skLineSegment(sketch, "E456", {"start": v(-12.7, -36.28) * mm, "end": v(-12.7, 6.35) * mm});
            skLineSegment(sketch, "E457", {"start": v(12.7, -41.36) * mm, "end": v(12.7, 6.35) * mm});
            skLineSegment(sketch, "E458", {"start": v(-12.7, -36.28) * mm, "end": v(12.7, -36.28) * mm});
            skLineSegment(sketch, "E459", {"start": v(-12.7, 6.35) * mm, "end": v(12.7, 6.35) * mm});
            skLineSegment(sketch, "E460", {"start": v(-8.04, -41.36) * mm, "end": v(-8.04, -36.28) * mm, "construction": true});
            skLineSegment(sketch, "E461", {"start": v(12.7, 6.35) * mm, "end": v(19.05, 6.35) * mm});
            skLineSegment(sketch, "E462", {"start": v(-12.7, 6.35) * mm, "end": v(-19.05, 6.35) * mm});
            skSolve(sketch);
        }
        {
            var Q0;
            Q0 = qSketchRegion(id + "F19", true);
            extrude(context, id + "F20", {"entities" : qUnion([Q0]), "operationType" : NewBodyOperationType.REMOVE, "endBound" : BoundingType.SYMMETRIC, "oppositeDirection" : true, "depth" : 5080 * mm, "offsetDistance" : 25.4 * mm});
        }
        {
            var Q0;
            Q0=makeQuery(id+"F9.boolean.opBoolean","MERGE",FACE,{"derivedFrom":[makeQuery(id+"F5.opExtrude","SWEPT_FACE",FACE,{"disambiguationData":[OSD([sQuery(id+"F0.wireOp",EDGE,"E1")])]})],"fromTools":[makeQuery(id+"F9.opExtrude","SWEPT_FACE",FACE,{"disambiguationData":[OSD([sQuery(id+"F8.wireOp",EDGE,"E215")])]})]});
            var sketch = newSketch(context, id + "F21", { "sketchPlane" : qUnion([Q0])});
            skLineSegment(sketch, "E463.0.0", {"start": v(-83.68, 19.05) * mm, "end": v(-83.68, -19.05) * mm, "construction": true});
            skLineSegment(sketch, "E463.0.1", {"start": v(-83.68, -19.05) * mm, "end": v(-54.36, -19.05) * mm, "construction": true});
            skLineSegment(sketch, "E463.0.2", {"start": v(-54.36, -19.05) * mm, "end": v(-54.36, 19.05) * mm, "construction": true});
            skLineSegment(sketch, "E463.0.3", {"start": v(-54.36, 19.05) * mm, "end": v(-83.68, 19.05) * mm, "construction": true});
            skLineSegment(sketch, "E464.0.0", {"start": v(-50.7, 19.05) * mm, "end": v(-54.36, 19.05) * mm, "construction": true});
            skLineSegment(sketch, "E464.0.1", {"start": v(-54.36, 19.05) * mm, "end": v(-54.36, -19.05) * mm, "construction": true});
            skLineSegment(sketch, "E464.0.2", {"start": v(-54.36, -19.05) * mm, "end": v(-50.7, -19.05) * mm, "construction": true});
            skLineSegment(sketch, "E464.0.3", {"start": v(-50.7, -19.05) * mm, "end": v(-50.7, 19.05) * mm, "construction": true});
            skLineSegment(sketch, "E465.0.0", {"start": v(34.64, 19.05) * mm, "end": v(-50.7, 19.05) * mm, "construction": true});
            skLineSegment(sketch, "E465.0.1", {"start": v(-50.7, 19.05) * mm, "end": v(-50.7, -19.05) * mm, "construction": true});
            skLineSegment(sketch, "E465.0.2", {"start": v(-50.7, -19.05) * mm, "end": v(34.64, -19.05) * mm, "construction": true});
            skFitSpline(sketch, "E465.0.3", {"points": [v(34.64, -19.05) * mm, v(34.64, -6.35) * mm, v(34.64, 6.35) * mm, v(34.64, 19.05) * mm], "construction": true});
            skLineSegment(sketch, "E466.0.0", {"start": v(34.6, 19.05) * mm, "end": v(34.6, -19.05) * mm, "construction": true});
            skLineSegment(sketch, "E466.0.1", {"start": v(34.6, -19.05) * mm, "end": v(37.3, -19.05) * mm, "construction": true});
            skLineSegment(sketch, "E466.0.2", {"start": v(37.3, -19.05) * mm, "end": v(37.3, 19.05) * mm, "construction": true});
            skLineSegment(sketch, "E466.0.3", {"start": v(37.3, 19.05) * mm, "end": v(34.6, 19.05) * mm, "construction": true});
            skLineSegment(sketch, "E467", {"start": v(66.63, 0) * mm, "end": v(-111.17, 0) * mm, "construction": true});
            skLineSegment(sketch, "E468", {"start": v(-22.27, 19.05) * mm, "end": v(-22.27, 0) * mm, "construction": true});
            skLineSegment(sketch, "E469.0.0", {"start": v(-111.17, 19.05) * mm, "end": v(-111.17, 12.7) * mm, "construction": true});
            skLineSegment(sketch, "E469.0.1", {"start": v(-111.17, 12.7) * mm, "end": v(-86.61, 12.7) * mm, "construction": true});
            skLineSegment(sketch, "E469.0.2", {"start": v(-86.61, 12.7) * mm, "end": v(-86.61, -12.7) * mm, "construction": true});
            skLineSegment(sketch, "E469.0.3", {"start": v(-86.61, -12.7) * mm, "end": v(-111.17, -12.7) * mm, "construction": true});
            skLineSegment(sketch, "E469.0.4", {"start": v(-111.17, -12.7) * mm, "end": v(-111.17, -19.05) * mm, "construction": true});
            skLineSegment(sketch, "E469.0.5", {"start": v(-111.17, -19.05) * mm, "end": v(-83.68, -19.05) * mm, "construction": true});
            skLineSegment(sketch, "E469.0.6", {"start": v(-83.68, -19.05) * mm, "end": v(-83.68, 19.05) * mm, "construction": true});
            skLineSegment(sketch, "E469.0.7", {"start": v(-83.68, 19.05) * mm, "end": v(-111.17, 19.05) * mm, "construction": true});
            skLineSegment(sketch, "E470.0.0", {"start": v(40.24, -12.7) * mm, "end": v(40.24, 12.7) * mm, "construction": true});
            skLineSegment(sketch, "E470.0.1", {"start": v(40.24, 12.7) * mm, "end": v(50.15, 12.7) * mm, "construction": true});
            skLineSegment(sketch, "E470.0.2", {"start": v(50.15, 12.7) * mm, "end": v(50.15, 19.05) * mm, "construction": true});
            skLineSegment(sketch, "E470.0.3", {"start": v(50.15, 19.05) * mm, "end": v(37.3, 19.05) * mm, "construction": true});
            skLineSegment(sketch, "E470.0.4", {"start": v(37.3, 19.05) * mm, "end": v(37.3, -19.05) * mm, "construction": true});
            skLineSegment(sketch, "E470.0.5", {"start": v(37.3, -19.05) * mm, "end": v(50.15, -19.05) * mm, "construction": true});
            skLineSegment(sketch, "E470.0.6", {"start": v(50.15, -19.05) * mm, "end": v(50.15, -12.7) * mm, "construction": true});
            skLineSegment(sketch, "E470.0.7", {"start": v(50.15, -12.7) * mm, "end": v(40.24, -12.7) * mm, "construction": true});
            skLineSegment(sketch, "E471.0.0", {"start": v(64.83, -12.7) * mm, "end": v(50.17, -12.7) * mm, "construction": true});
            skLineSegment(sketch, "E471.0.1", {"start": v(50.17, -12.7) * mm, "end": v(50.17, -19.05) * mm, "construction": true});
            skLineSegment(sketch, "E471.0.2", {"start": v(50.17, -19.05) * mm, "end": v(64.83, -19.05) * mm, "construction": true});
            skLineSegment(sketch, "E471.0.3", {"start": v(64.83, -19.05) * mm, "end": v(64.83, -12.7) * mm, "construction": true});
            skLineSegment(sketch, "E472.0.0", {"start": v(50.17, 12.7) * mm, "end": v(64.83, 12.7) * mm, "construction": true});
            skLineSegment(sketch, "E472.0.1", {"start": v(64.83, 12.7) * mm, "end": v(64.83, 19.05) * mm, "construction": true});
            skLineSegment(sketch, "E472.0.2", {"start": v(64.83, 19.05) * mm, "end": v(50.17, 19.05) * mm, "construction": true});
            skLineSegment(sketch, "E472.0.3", {"start": v(50.17, 19.05) * mm, "end": v(50.17, 12.7) * mm, "construction": true});
            skLineSegment(sketch, "E473.0.0", {"start": v(66.63, -19.05) * mm, "end": v(66.63, 19.05) * mm, "construction": true});
            skLineSegment(sketch, "E473.0.1", {"start": v(66.63, 19.05) * mm, "end": v(64.83, 19.05) * mm, "construction": true});
            skLineSegment(sketch, "E473.0.2", {"start": v(64.83, 19.05) * mm, "end": v(64.83, 12.7) * mm, "construction": true});
            skLineSegment(sketch, "E473.0.3", {"start": v(64.83, 12.7) * mm, "end": v(-111.17, 12.7) * mm, "construction": true});
            skLineSegment(sketch, "E473.0.4", {"start": v(-111.17, 12.7) * mm, "end": v(-111.17, -12.7) * mm, "construction": true});
            skLineSegment(sketch, "E473.0.5", {"start": v(-111.17, -12.7) * mm, "end": v(64.83, -12.7) * mm, "construction": true});
            skLineSegment(sketch, "E473.0.6", {"start": v(64.83, -12.7) * mm, "end": v(64.83, -19.05) * mm, "construction": true});
            skLineSegment(sketch, "E473.0.7", {"start": v(64.83, -19.05) * mm, "end": v(66.63, -19.05) * mm, "construction": true});
            skLineSegment(sketch, "E474", {"start": v(-22.27, 19.05) * mm, "end": v(-22.27, -19.05) * mm, "construction": true});
            skLineSegment(sketch, "E475.bottom", {"start": v(-9.57, -12.7) * mm, "end": v(-34.97, -12.7) * mm});
            skLineSegment(sketch, "E475.top", {"start": v(-9.57, 12.7) * mm, "end": v(-34.97, 12.7) * mm});
            skLineSegment(sketch, "E475.left", {"start": v(-9.57, -12.7) * mm, "end": v(-9.57, 12.7) * mm});
            skLineSegment(sketch, "E475.right", {"start": v(-34.97, -12.7) * mm, "end": v(-34.97, 12.7) * mm});
            skPoint(sketch, "E475.middle", {"position": v(-22.27, 0) * mm});
            skSolve(sketch);
        }
        {
            var Q0;
            Q0 = qSketchRegion(id + "F21", true);
            extrude(context, id + "F22", {"entities" : qUnion([Q0]), "operationType" : NewBodyOperationType.REMOVE, "depth" : 508 * mm, "offsetDistance" : 25.4 * mm});
        }
        {
            var Q0;
            Q0=makeQuery(id+"F18.opExtrude","SWEPT_BODY",BODY,{"disambiguationData":[OSD([sQuery(id+"F15.wireOp",EDGE,"E309"),sQuery(id+"F15.wireOp",EDGE,"E310"),sQuery(id+"F15.wireOp",EDGE,"E311"),sQuery(id+"F15.wireOp",EDGE,"E312"),sQuery(id+"F15.wireOp",EDGE,"E314"),sQuery(id+"F15.wireOp",EDGE,"E315"),sQuery(id+"F15.wireOp",EDGE,"E316.MirrorCS"),sQuery(id+"F15.wireOp",EDGE,"E318.MirrorCS"),sQuery(id+"F15.wireOp",EDGE,"E319.MirrorCS"),sQuery(id+"F15.wireOp",EDGE,"E320.MirrorCS"),sQuery(id+"F15.wireOp",EDGE,"E321.MirrorCS"),sQuery(id+"F15.wireOp",EDGE,"E322.MirrorCS"),sQuery(id+"F15.wireOp",EDGE,"E324.MirrorCS"),sQuery(id+"F15.wireOp",EDGE,"E325.MirrorCS"),sQuery(id+"F15.wireOp",EDGE,"E326.MirrorCS"),sQuery(id+"F15.wireOp",EDGE,"E327.MirrorCS"),sQuery(id+"F15.wireOp",EDGE,"E329.MirrorCS"),sQuery(id+"F15.wireOp",EDGE,"E330.MirrorCS"),sQuery(id+"F15.wireOp",EDGE,"E332.MirrorCS"),sQuery(id+"F15.wireOp",EDGE,"E333.MirrorCS"),sQuery(id+"F15.wireOp",EDGE,"E334.MirrorCS"),sQuery(id+"F15.wireOp",EDGE,"E335.MirrorCS"),sQuery(id+"F15.wireOp",EDGE,"E336.MirrorCS"),sQuery(id+"F15.wireOp",EDGE,"E337.MirrorCS"),sQuery(id+"F15.wireOp",EDGE,"E339.MirrorCS"),sQuery(id+"F15.wireOp",EDGE,"E340.MirrorCS"),sQuery(id+"F15.wireOp",EDGE,"E341.MirrorCS"),sQuery(id+"F15.wireOp",EDGE,"E343.MirrorCS"),sQuery(id+"F15.wireOp",EDGE,"E344.MirrorCS"),sQuery(id+"F15.wireOp",EDGE,"E345.MirrorCS"),sQuery(id+"F15.wireOp",EDGE,"E346.MirrorCS"),sQuery(id+"F15.wireOp",EDGE,"E347.MirrorCS"),sQuery(id+"F15.wireOp",EDGE,"E349.MirrorCS"),sQuery(id+"F15.wireOp",EDGE,"E350.MirrorCS"),sQuery(id+"F15.wireOp",EDGE,"E351.MirrorCS"),sQuery(id+"F15.wireOp",EDGE,"E353.MirrorCS"),sQuery(id+"F15.wireOp",EDGE,"E354.MirrorCS"),sQuery(id+"F15.wireOp",EDGE,"E355.MirrorCS"),sQuery(id+"F15.wireOp",EDGE,"E356.MirrorCS"),sQuery(id+"F15.wireOp",EDGE,"E357.MirrorCS"),sQuery(id+"F15.wireOp",EDGE,"E358.MirrorCS"),sQuery(id+"F15.wireOp",EDGE,"E360"),sQuery(id+"F15.wireOp",EDGE,"E362"),sQuery(id+"F15.wireOp",EDGE,"E363"),sQuery(id+"F15.wireOp",EDGE,"E364"),sQuery(id+"F15.wireOp",EDGE,"E366"),sQuery(id+"F15.wireOp",EDGE,"E368.MirrorCS"),sQuery(id+"F15.wireOp",EDGE,"E369.MirrorCS"),sQuery(id+"F15.wireOp",EDGE,"E370.MirrorCS"),sQuery(id+"F15.wireOp",EDGE,"E371.MirrorCS"),sQuery(id+"F15.wireOp",EDGE,"E372.MirrorCS"),sQuery(id+"F15.wireOp",EDGE,"E373.MirrorCS"),sQuery(id+"F15.wireOp",EDGE,"E374.MirrorCS"),sQuery(id+"F15.wireOp",EDGE,"E375.MirrorCS"),sQuery(id+"F15.wireOp",EDGE,"E377.MirrorCS"),sQuery(id+"F15.wireOp",EDGE,"E379.MirrorCS"),sQuery(id+"F15.wireOp",EDGE,"E380.MirrorCS"),sQuery(id+"F15.wireOp",EDGE,"E381.MirrorCS"),sQuery(id+"F15.wireOp",EDGE,"E382.MirrorCS"),sQuery(id+"F15.wireOp",EDGE,"E383.MirrorCS"),sQuery(id+"F15.wireOp",EDGE,"E384.MirrorCS"),sQuery(id+"F15.wireOp",EDGE,"E385.MirrorCS"),sQuery(id+"F15.wireOp",EDGE,"E386.MirrorCS"),sQuery(id+"F15.wireOp",EDGE,"E387.MirrorCS"),sQuery(id+"F15.wireOp",EDGE,"E388.MirrorCS"),sQuery(id+"F15.wireOp",EDGE,"E389.MirrorCS"),sQuery(id+"F15.wireOp",EDGE,"E390.MirrorCS"),sQuery(id+"F15.wireOp",EDGE,"E391.MirrorCS"),sQuery(id+"F15.wireOp",EDGE,"E394.MirrorCS"),sQuery(id+"F15.wireOp",EDGE,"E396.MirrorCS"),sQuery(id+"F15.wireOp",EDGE,"E397.MirrorCS"),sQuery(id+"F15.wireOp",EDGE,"E399.MirrorCS"),sQuery(id+"F15.wireOp",EDGE,"E402.MirrorCS"),sQuery(id+"F15.wireOp",EDGE,"E403.MirrorCS"),sQuery(id+"F15.wireOp",EDGE,"E405.MirrorCS"),sQuery(id+"F15.wireOp",EDGE,"E406.MirrorCS"),sQuery(id+"F15.wireOp",EDGE,"E409.MirrorCS"),sQuery(id+"F15.wireOp",EDGE,"E413.MirrorCS"),sQuery(id+"F15.wireOp",EDGE,"E414.MirrorCS"),sQuery(id+"F15.wireOp",EDGE,"E417.MirrorCS"),sQuery(id+"F15.wireOp",EDGE,"E418.MirrorCS"),sQuery(id+"F15.wireOp",EDGE,"E420.MirrorCS"),sQuery(id+"F15.wireOp",EDGE,"E421.MirrorCS"),sQuery(id+"F15.wireOp",EDGE,"E423.MirrorCS"),sQuery(id+"F15.wireOp",EDGE,"E427.MirrorCS"),sQuery(id+"F15.wireOp",EDGE,"E429.MirrorCS"),sQuery(id+"F15.wireOp",EDGE,"E431.MirrorCS"),sQuery(id+"F15.wireOp",EDGE,"E432.MirrorCS"),sQuery(id+"F15.wireOp",EDGE,"E433.MirrorCS"),sQuery(id+"F15.wireOp",EDGE,"E434.MirrorCS"),sQuery(id+"F15.wireOp",EDGE,"E436.MirrorCS"),sQuery(id+"F15.wireOp",EDGE,"E437.MirrorCS"),sQuery(id+"F15.wireOp",EDGE,"E438.MirrorCS")])]});
            var Q1;
            Q1=makeQuery(id+"F18.opExtrude","CAP_VERTEX",VERTEX,{"disambiguationData":[OSD([sQuery(id+"F15.wireOp",EDGE,"E329.MirrorCS"),sQuery(id+"F15.wireOp",EDGE,"E405.MirrorCS")])],"isStart":false});
            transform(context, id + "F23", {"entities" : qUnion([Q0]), "transformType" : TransformType.SCALE_UNIFORMLY, "scale" : 1.05, "scalePoint" : qUnion([Q1]), "makeCopy" : false});
        }
        {
            var Q0;
            Q0=makeQuery(id+"F18.opExtrude","SWEPT_BODY",BODY,{"disambiguationData":[OSD([sQuery(id+"F15.wireOp",EDGE,"E309"),sQuery(id+"F15.wireOp",EDGE,"E310"),sQuery(id+"F15.wireOp",EDGE,"E311"),sQuery(id+"F15.wireOp",EDGE,"E312"),sQuery(id+"F15.wireOp",EDGE,"E314"),sQuery(id+"F15.wireOp",EDGE,"E315"),sQuery(id+"F15.wireOp",EDGE,"E316.MirrorCS"),sQuery(id+"F15.wireOp",EDGE,"E318.MirrorCS"),sQuery(id+"F15.wireOp",EDGE,"E319.MirrorCS"),sQuery(id+"F15.wireOp",EDGE,"E320.MirrorCS"),sQuery(id+"F15.wireOp",EDGE,"E321.MirrorCS"),sQuery(id+"F15.wireOp",EDGE,"E322.MirrorCS"),sQuery(id+"F15.wireOp",EDGE,"E324.MirrorCS"),sQuery(id+"F15.wireOp",EDGE,"E325.MirrorCS"),sQuery(id+"F15.wireOp",EDGE,"E326.MirrorCS"),sQuery(id+"F15.wireOp",EDGE,"E327.MirrorCS"),sQuery(id+"F15.wireOp",EDGE,"E329.MirrorCS"),sQuery(id+"F15.wireOp",EDGE,"E330.MirrorCS"),sQuery(id+"F15.wireOp",EDGE,"E332.MirrorCS"),sQuery(id+"F15.wireOp",EDGE,"E333.MirrorCS"),sQuery(id+"F15.wireOp",EDGE,"E334.MirrorCS"),sQuery(id+"F15.wireOp",EDGE,"E335.MirrorCS"),sQuery(id+"F15.wireOp",EDGE,"E336.MirrorCS"),sQuery(id+"F15.wireOp",EDGE,"E337.MirrorCS"),sQuery(id+"F15.wireOp",EDGE,"E339.MirrorCS"),sQuery(id+"F15.wireOp",EDGE,"E340.MirrorCS"),sQuery(id+"F15.wireOp",EDGE,"E341.MirrorCS"),sQuery(id+"F15.wireOp",EDGE,"E343.MirrorCS"),sQuery(id+"F15.wireOp",EDGE,"E344.MirrorCS"),sQuery(id+"F15.wireOp",EDGE,"E345.MirrorCS"),sQuery(id+"F15.wireOp",EDGE,"E346.MirrorCS"),sQuery(id+"F15.wireOp",EDGE,"E347.MirrorCS"),sQuery(id+"F15.wireOp",EDGE,"E349.MirrorCS"),sQuery(id+"F15.wireOp",EDGE,"E350.MirrorCS"),sQuery(id+"F15.wireOp",EDGE,"E351.MirrorCS"),sQuery(id+"F15.wireOp",EDGE,"E353.MirrorCS"),sQuery(id+"F15.wireOp",EDGE,"E354.MirrorCS"),sQuery(id+"F15.wireOp",EDGE,"E355.MirrorCS"),sQuery(id+"F15.wireOp",EDGE,"E356.MirrorCS"),sQuery(id+"F15.wireOp",EDGE,"E357.MirrorCS"),sQuery(id+"F15.wireOp",EDGE,"E358.MirrorCS"),sQuery(id+"F15.wireOp",EDGE,"E360"),sQuery(id+"F15.wireOp",EDGE,"E362"),sQuery(id+"F15.wireOp",EDGE,"E363"),sQuery(id+"F15.wireOp",EDGE,"E364"),sQuery(id+"F15.wireOp",EDGE,"E366"),sQuery(id+"F15.wireOp",EDGE,"E368.MirrorCS"),sQuery(id+"F15.wireOp",EDGE,"E369.MirrorCS"),sQuery(id+"F15.wireOp",EDGE,"E370.MirrorCS"),sQuery(id+"F15.wireOp",EDGE,"E371.MirrorCS"),sQuery(id+"F15.wireOp",EDGE,"E372.MirrorCS"),sQuery(id+"F15.wireOp",EDGE,"E373.MirrorCS"),sQuery(id+"F15.wireOp",EDGE,"E374.MirrorCS"),sQuery(id+"F15.wireOp",EDGE,"E375.MirrorCS"),sQuery(id+"F15.wireOp",EDGE,"E377.MirrorCS"),sQuery(id+"F15.wireOp",EDGE,"E379.MirrorCS"),sQuery(id+"F15.wireOp",EDGE,"E380.MirrorCS"),sQuery(id+"F15.wireOp",EDGE,"E381.MirrorCS"),sQuery(id+"F15.wireOp",EDGE,"E382.MirrorCS"),sQuery(id+"F15.wireOp",EDGE,"E383.MirrorCS"),sQuery(id+"F15.wireOp",EDGE,"E384.MirrorCS"),sQuery(id+"F15.wireOp",EDGE,"E385.MirrorCS"),sQuery(id+"F15.wireOp",EDGE,"E386.MirrorCS"),sQuery(id+"F15.wireOp",EDGE,"E387.MirrorCS"),sQuery(id+"F15.wireOp",EDGE,"E388.MirrorCS"),sQuery(id+"F15.wireOp",EDGE,"E389.MirrorCS"),sQuery(id+"F15.wireOp",EDGE,"E390.MirrorCS"),sQuery(id+"F15.wireOp",EDGE,"E391.MirrorCS"),sQuery(id+"F15.wireOp",EDGE,"E394.MirrorCS"),sQuery(id+"F15.wireOp",EDGE,"E396.MirrorCS"),sQuery(id+"F15.wireOp",EDGE,"E397.MirrorCS"),sQuery(id+"F15.wireOp",EDGE,"E399.MirrorCS"),sQuery(id+"F15.wireOp",EDGE,"E402.MirrorCS"),sQuery(id+"F15.wireOp",EDGE,"E403.MirrorCS"),sQuery(id+"F15.wireOp",EDGE,"E405.MirrorCS"),sQuery(id+"F15.wireOp",EDGE,"E406.MirrorCS"),sQuery(id+"F15.wireOp",EDGE,"E409.MirrorCS"),sQuery(id+"F15.wireOp",EDGE,"E413.MirrorCS"),sQuery(id+"F15.wireOp",EDGE,"E414.MirrorCS"),sQuery(id+"F15.wireOp",EDGE,"E417.MirrorCS"),sQuery(id+"F15.wireOp",EDGE,"E418.MirrorCS"),sQuery(id+"F15.wireOp",EDGE,"E420.MirrorCS"),sQuery(id+"F15.wireOp",EDGE,"E421.MirrorCS"),sQuery(id+"F15.wireOp",EDGE,"E423.MirrorCS"),sQuery(id+"F15.wireOp",EDGE,"E427.MirrorCS"),sQuery(id+"F15.wireOp",EDGE,"E429.MirrorCS"),sQuery(id+"F15.wireOp",EDGE,"E431.MirrorCS"),sQuery(id+"F15.wireOp",EDGE,"E432.MirrorCS"),sQuery(id+"F15.wireOp",EDGE,"E433.MirrorCS"),sQuery(id+"F15.wireOp",EDGE,"E434.MirrorCS"),sQuery(id+"F15.wireOp",EDGE,"E436.MirrorCS"),sQuery(id+"F15.wireOp",EDGE,"E437.MirrorCS"),sQuery(id+"F15.wireOp",EDGE,"E438.MirrorCS")])]});
            var Q1;
            Q1=makeQuery(id+"F5.opExtrude","SWEPT_BODY",BODY,{"disambiguationData":[OSD([sQuery(id+"F0.wireOp",EDGE,"E0.0.11"),sQuery(id+"F0.wireOp",EDGE,"E0.0.13"),sQuery(id+"F0.wireOp",EDGE,"E1"),sQuery(id+"F0.wireOp",EDGE,"E2")])]});
            booleanBodies(context, id + "F24", {"operationType" : BooleanOperationType.UNION, "tools" : qUnion([Q0, Q1])});
        }
        {
            var Q0;
            Q0=makeQuery(id+"F24.opBoolean","MERGE",FACE,{"derivedFrom":[makeQuery(id+"F17.boolean.opBoolean","MERGE",FACE,{"derivedFrom":[makeQuery(id+"F14.boolean.opBoolean","MERGE",FACE,{"derivedFrom":[makeQuery(id+"F7.boolean.opBoolean","MERGE",FACE,{"derivedFrom":[makeQuery(id+"F6.boolean.opBoolean","MERGE",FACE,{"derivedFrom":[makeQuery(id+"F5.opExtrude","CAP_FACE",FACE,{"disambiguationData":[OSD([sQuery(id+"F0.wireOp",EDGE,"E0.0.11"),sQuery(id+"F0.wireOp",EDGE,"E0.0.13"),sQuery(id+"F0.wireOp",EDGE,"E1"),sQuery(id+"F0.wireOp",EDGE,"E2")])],"isStart":false}),makeQuery(id+"F6.opExtrude","CAP_FACE",FACE,{"disambiguationData":[OSD([sQuery(id+"F1.wireOp",EDGE,"E3"),sQuery(id+"F1.wireOp",EDGE,"E4"),sQuery(id+"F1.wireOp",EDGE,"E5"),sQuery(id+"F1.wireOp",EDGE,"E8.1"),sQuery(id+"F1.wireOp",EDGE,"E8.2"),sQuery(id+"F1.wireOp",EDGE,"E10.0"),sQuery(id+"F1.wireOp",EDGE,"E10.1"),sQuery(id+"F1.wireOp",EDGE,"E10.2"),sQuery(id+"F1.wireOp",EDGE,"E11"),sQuery(id+"F1.wireOp",EDGE,"E20.1.0.0"),sQuery(id+"F1.wireOp",EDGE,"E20.1.0.2"),sQuery(id+"F1.wireOp",EDGE,"E20.1.0.4"),sQuery(id+"F1.wireOp",EDGE,"E20.1.0.9"),sQuery(id+"F1.wireOp",EDGE,"E20.1.0.11"),sQuery(id+"F1.wireOp",EDGE,"E29.MirrorCS"),sQuery(id+"F1.wireOp",EDGE,"E31.MirrorCS"),sQuery(id+"F1.wireOp",EDGE,"E34.MirrorCS"),sQuery(id+"F1.wireOp",EDGE,"E37.MirrorCS"),sQuery(id+"F1.wireOp",EDGE,"E38.MirrorCS"),sQuery(id+"F1.wireOp",EDGE,"E49.MirrorCS"),sQuery(id+"F1.wireOp",EDGE,"E53.MirrorCS"),sQuery(id+"F1.wireOp",EDGE,"E55.MirrorCS"),sQuery(id+"F1.wireOp",EDGE,"E57.MirrorCS"),sQuery(id+"F1.wireOp",EDGE,"E59.MirrorCS"),sQuery(id+"F1.wireOp",EDGE,"E61.MirrorCS"),sQuery(id+"F1.wireOp",EDGE,"E71.MirrorCS"),sQuery(id+"F1.wireOp",EDGE,"E73.MirrorCS"),sQuery(id+"F1.wireOp",EDGE,"E74.MirrorCS"),sQuery(id+"F1.wireOp",EDGE,"E75.MirrorCS"),sQuery(id+"F1.wireOp",EDGE,"E77.MirrorCS"),sQuery(id+"F1.wireOp",EDGE,"E78.MirrorCS"),sQuery(id+"F1.wireOp",EDGE,"E83.MirrorCS"),sQuery(id+"F1.wireOp",EDGE,"E86.MirrorCS"),sQuery(id+"F1.wireOp",EDGE,"E91.MirrorCS")])],"isStart":false}),makeQuery(id+"F6.opExtrude","CAP_FACE",FACE,{"disambiguationData":[OSD([sQuery(id+"F2.wireOp",EDGE,"E92.2"),sQuery(id+"F2.wireOp",EDGE,"E93.0.6"),sQuery(id+"F2.wireOp",EDGE,"E93.0.7"),sQuery(id+"F2.wireOp",EDGE,"E93.0.8"),sQuery(id+"F2.wireOp",EDGE,"E96.0"),sQuery(id+"F2.wireOp",EDGE,"E96.1"),sQuery(id+"F2.wireOp",EDGE,"E96.2"),sQuery(id+"F2.wireOp",EDGE,"E106.1.0.1"),sQuery(id+"F2.wireOp",EDGE,"E106.1.0.4"),sQuery(id+"F2.wireOp",EDGE,"E106.1.0.5"),sQuery(id+"F2.wireOp",EDGE,"E106.1.0.6"),sQuery(id+"F2.wireOp",EDGE,"E106.2.0.1"),sQuery(id+"F2.wireOp",EDGE,"E106.2.0.4"),sQuery(id+"F2.wireOp",EDGE,"E106.2.0.5"),sQuery(id+"F2.wireOp",EDGE,"E106.2.0.6"),sQuery(id+"F2.wireOp",EDGE,"E107"),sQuery(id+"F2.wireOp",EDGE,"E108"),sQuery(id+"F2.wireOp",EDGE,"E109"),sQuery(id+"F2.wireOp",EDGE,"E110"),sQuery(id+"F2.wireOp",EDGE,"E111"),sQuery(id+"F2.wireOp",EDGE,"E112"),sQuery(id+"F2.wireOp",EDGE,"E113"),sQuery(id+"F2.wireOp",EDGE,"E114"),sQuery(id+"F2.wireOp",EDGE,"E115"),sQuery(id+"F2.wireOp",EDGE,"E116")])],"isStart":false})]}),makeQuery(id+"F7.opExtrude","CAP_FACE",FACE,{"disambiguationData":[OSD([sQuery(id+"F3.wireOp",EDGE,"E117.0.0"),sQuery(id+"F3.wireOp",EDGE,"E117.0.1"),sQuery(id+"F3.wireOp",EDGE,"E117.0.2"),sQuery(id+"F3.wireOp",EDGE,"E117.0.3"),sQuery(id+"F3.wireOp",EDGE,"E184"),sQuery(id+"F3.wireOp",EDGE,"E185"),sQuery(id+"F3.wireOp",EDGE,"E186")])],"isStart":false}),makeQuery(id+"F7.opExtrude","CAP_FACE",FACE,{"disambiguationData":[OSD([sQuery(id+"F3.wireOp",EDGE,"E118.0.0"),sQuery(id+"F3.wireOp",EDGE,"E118.0.1"),sQuery(id+"F3.wireOp",EDGE,"E118.0.2"),sQuery(id+"F3.wireOp",EDGE,"E118.0.3"),sQuery(id+"F3.wireOp",EDGE,"E118.0.4")])],"isStart":false}),makeQuery(id+"F7.opExtrude","CAP_FACE",FACE,{"disambiguationData":[OSD([sQuery(id+"F3.wireOp",EDGE,"E119.MirrorCS"),sQuery(id+"F3.wireOp",EDGE,"E120.MirrorCS"),sQuery(id+"F3.wireOp",EDGE,"E121.MirrorCS"),sQuery(id+"F3.wireOp",EDGE,"E122.MirrorCS"),sQuery(id+"F3.wireOp",EDGE,"E123.MirrorCS")])],"isStart":false}),makeQuery(id+"F7.opExtrude","CAP_FACE",FACE,{"disambiguationData":[OSD([sQuery(id+"F3.wireOp",EDGE,"E128.MirrorCS"),sQuery(id+"F3.wireOp",EDGE,"E129.MirrorCS"),sQuery(id+"F3.wireOp",EDGE,"E130.MirrorCS"),sQuery(id+"F3.wireOp",EDGE,"E131.MirrorCS"),sQuery(id+"F3.wireOp",EDGE,"E132.MirrorCS")])],"isStart":false}),makeQuery(id+"F7.opExtrude","CAP_FACE",FACE,{"disambiguationData":[OSD([sQuery(id+"F3.wireOp",EDGE,"E133.MirrorCS"),sQuery(id+"F3.wireOp",EDGE,"E151.MirrorCS"),sQuery(id+"F3.wireOp",EDGE,"E152.MirrorCS"),sQuery(id+"F3.wireOp",EDGE,"E153.MirrorCS"),sQuery(id+"F3.wireOp",EDGE,"E154.MirrorCS"),sQuery(id+"F3.wireOp",EDGE,"E156.MirrorCS"),sQuery(id+"F3.wireOp",EDGE,"E157.0"),sQuery(id+"F3.wireOp",EDGE,"E159"),sQuery(id+"F3.wireOp",EDGE,"E160.0"),sQuery(id+"F3.wireOp",EDGE,"E162"),sQuery(id+"F3.wireOp",EDGE,"E163"),sQuery(id+"F3.wireOp",EDGE,"E164"),sQuery(id+"F3.wireOp",EDGE,"E166"),sQuery(id+"F3.wireOp",EDGE,"E167"),sQuery(id+"F3.wireOp",EDGE,"E169"),sQuery(id+"F3.wireOp",EDGE,"E170"),sQuery(id+"F3.wireOp",EDGE,"E171"),sQuery(id+"F3.wireOp",EDGE,"E172"),sQuery(id+"F3.wireOp",EDGE,"E173"),sQuery(id+"F3.wireOp",EDGE,"E178.MirrorCS"),sQuery(id+"F3.wireOp",EDGE,"E179.MirrorCS"),sQuery(id+"F3.wireOp",EDGE,"E181.MirrorCS"),sQuery(id+"F3.wireOp",EDGE,"E182.MirrorCS"),sQuery(id+"F3.wireOp",EDGE,"E183.MirrorCS"),sQuery(id+"F3.wireOp",EDGE,"E187.MirrorCS"),sQuery(id+"F3.wireOp",EDGE,"E188.MirrorCS"),sQuery(id+"F3.wireOp",EDGE,"E189.MirrorCS"),sQuery(id+"F3.wireOp",EDGE,"E190"),sQuery(id+"F3.wireOp",EDGE,"E191"),sQuery(id+"F3.wireOp",EDGE,"E193.MirrorCS"),sQuery(id+"F3.wireOp",EDGE,"E195.MirrorCS"),sQuery(id+"F3.wireOp",EDGE,"E197"),sQuery(id+"F3.wireOp",EDGE,"E198"),sQuery(id+"F3.wireOp",EDGE,"E199"),sQuery(id+"F3.wireOp",EDGE,"E200"),sQuery(id+"F3.wireOp",EDGE,"E201"),sQuery(id+"F3.wireOp",EDGE,"E203"),sQuery(id+"F3.wireOp",EDGE,"E204"),sQuery(id+"F3.wireOp",EDGE,"E208"),sQuery(id+"F3.wireOp",EDGE,"E209")])],"isStart":false}),makeQuery(id+"F7.opExtrude","CAP_FACE",FACE,{"disambiguationData":[OSD([sQuery(id+"F3.wireOp",EDGE,"E135.MirrorCS"),sQuery(id+"F3.wireOp",EDGE,"E136.MirrorCS"),sQuery(id+"F3.wireOp",EDGE,"E137.MirrorCS"),sQuery(id+"F3.wireOp",EDGE,"E138.MirrorCS"),sQuery(id+"F3.wireOp",EDGE,"E145.MirrorCS"),sQuery(id+"F3.wireOp",EDGE,"E150.MirrorCS")])],"isStart":false}),makeQuery(id+"F7.opExtrude","CAP_FACE",FACE,{"disambiguationData":[OSD([sQuery(id+"F3.wireOp",EDGE,"E139.MirrorCS"),sQuery(id+"F3.wireOp",EDGE,"E141.MirrorCS"),sQuery(id+"F3.wireOp",EDGE,"E142.MirrorCS"),sQuery(id+"F3.wireOp",EDGE,"E147.MirrorCS"),sQuery(id+"F3.wireOp",EDGE,"E148.MirrorCS")])],"isStart":false}),makeQuery(id+"F7.opExtrude","CAP_FACE",FACE,{"disambiguationData":[OSD([sQuery(id+"F3.wireOp",EDGE,"E140.MirrorCS"),sQuery(id+"F3.wireOp",EDGE,"E143.MirrorCS"),sQuery(id+"F3.wireOp",EDGE,"E144.MirrorCS"),sQuery(id+"F3.wireOp",EDGE,"E146.MirrorCS"),sQuery(id+"F3.wireOp",EDGE,"E149.MirrorCS")])],"isStart":false}),makeQuery(id+"F7.opExtrude","CAP_FACE",FACE,{"disambiguationData":[OSD([sQuery(id+"F4.wireOp",EDGE,"E211.0"),sQuery(id+"F4.wireOp",EDGE,"E212.0"),sQuery(id+"F4.wireOp",EDGE,"E213"),sQuery(id+"F4.wireOp",EDGE,"E214")])],"isStart":false})]}),makeQuery(id+"F14.opExtrude","CAP_FACE",FACE,{"disambiguationData":[OSD([sQuery(id+"F12.wireOp",EDGE,"E227.1"),sQuery(id+"F12.wireOp",EDGE,"E228.1"),sQuery(id+"F12.wireOp",EDGE,"E229.0"),sQuery(id+"F12.wireOp",EDGE,"E230.1"),sQuery(id+"F12.wireOp",EDGE,"E232"),sQuery(id+"F12.wireOp",EDGE,"E233"),sQuery(id+"F12.wireOp",EDGE,"E241"),sQuery(id+"F12.wireOp",EDGE,"E242")])],"isStart":false})]}),makeQuery(id+"F17.opExtrude","CAP_FACE",FACE,{"disambiguationData":[OSD([sQuery(id+"F16.wireOp",EDGE,"E440.0.0"),sQuery(id+"F16.wireOp",EDGE,"E440.0.1"),sQuery(id+"F16.wireOp",EDGE,"E440.0.2"),sQuery(id+"F16.wireOp",EDGE,"E440.0.3"),sQuery(id+"F16.wireOp",EDGE,"E440.0.4"),sQuery(id+"F16.wireOp",EDGE,"E440.0.5"),sQuery(id+"F16.wireOp",EDGE,"E440.0.6"),sQuery(id+"F16.wireOp",EDGE,"E440.0.7"),sQuery(id+"F16.wireOp",EDGE,"E441.0.0"),sQuery(id+"F16.wireOp",EDGE,"E441.0.1"),sQuery(id+"F16.wireOp",EDGE,"E441.0.2"),sQuery(id+"F16.wireOp",EDGE,"E441.0.4")])],"isStart":false}),makeQuery(id+"F17.opExtrude","CAP_FACE",FACE,{"disambiguationData":[OSD([sQuery(id+"F16.wireOp",EDGE,"E442.MirrorCS"),sQuery(id+"F16.wireOp",EDGE,"E443.MirrorCS"),sQuery(id+"F16.wireOp",EDGE,"E444.MirrorCS"),sQuery(id+"F16.wireOp",EDGE,"E445.MirrorCS"),sQuery(id+"F16.wireOp",EDGE,"E447.MirrorCS"),sQuery(id+"F16.wireOp",EDGE,"E448.MirrorCS"),sQuery(id+"F16.wireOp",EDGE,"E449.MirrorCS"),sQuery(id+"F16.wireOp",EDGE,"E450.MirrorCS"),sQuery(id+"F16.wireOp",EDGE,"E452.MirrorCS"),sQuery(id+"F16.wireOp",EDGE,"E453.MirrorCS"),sQuery(id+"F16.wireOp",EDGE,"E454.MirrorCS"),sQuery(id+"F16.wireOp",EDGE,"E455.MirrorCS")])],"isStart":false})]}),makeQuery(id+"F18.opExtrude","CAP_FACE",FACE,{"disambiguationData":[OSD([sQuery(id+"F15.wireOp",EDGE,"E309"),sQuery(id+"F15.wireOp",EDGE,"E310"),sQuery(id+"F15.wireOp",EDGE,"E311"),sQuery(id+"F15.wireOp",EDGE,"E312"),sQuery(id+"F15.wireOp",EDGE,"E314"),sQuery(id+"F15.wireOp",EDGE,"E315"),sQuery(id+"F15.wireOp",EDGE,"E316.MirrorCS"),sQuery(id+"F15.wireOp",EDGE,"E318.MirrorCS"),sQuery(id+"F15.wireOp",EDGE,"E319.MirrorCS"),sQuery(id+"F15.wireOp",EDGE,"E320.MirrorCS"),sQuery(id+"F15.wireOp",EDGE,"E321.MirrorCS"),sQuery(id+"F15.wireOp",EDGE,"E322.MirrorCS"),sQuery(id+"F15.wireOp",EDGE,"E324.MirrorCS"),sQuery(id+"F15.wireOp",EDGE,"E325.MirrorCS"),sQuery(id+"F15.wireOp",EDGE,"E326.MirrorCS"),sQuery(id+"F15.wireOp",EDGE,"E327.MirrorCS"),sQuery(id+"F15.wireOp",EDGE,"E329.MirrorCS"),sQuery(id+"F15.wireOp",EDGE,"E330.MirrorCS"),sQuery(id+"F15.wireOp",EDGE,"E332.MirrorCS"),sQuery(id+"F15.wireOp",EDGE,"E333.MirrorCS"),sQuery(id+"F15.wireOp",EDGE,"E334.MirrorCS"),sQuery(id+"F15.wireOp",EDGE,"E335.MirrorCS"),sQuery(id+"F15.wireOp",EDGE,"E336.MirrorCS"),sQuery(id+"F15.wireOp",EDGE,"E337.MirrorCS"),sQuery(id+"F15.wireOp",EDGE,"E339.MirrorCS"),sQuery(id+"F15.wireOp",EDGE,"E340.MirrorCS"),sQuery(id+"F15.wireOp",EDGE,"E341.MirrorCS"),sQuery(id+"F15.wireOp",EDGE,"E343.MirrorCS"),sQuery(id+"F15.wireOp",EDGE,"E344.MirrorCS"),sQuery(id+"F15.wireOp",EDGE,"E345.MirrorCS"),sQuery(id+"F15.wireOp",EDGE,"E346.MirrorCS"),sQuery(id+"F15.wireOp",EDGE,"E347.MirrorCS"),sQuery(id+"F15.wireOp",EDGE,"E349.MirrorCS"),sQuery(id+"F15.wireOp",EDGE,"E350.MirrorCS"),sQuery(id+"F15.wireOp",EDGE,"E351.MirrorCS"),sQuery(id+"F15.wireOp",EDGE,"E353.MirrorCS"),sQuery(id+"F15.wireOp",EDGE,"E354.MirrorCS"),sQuery(id+"F15.wireOp",EDGE,"E355.MirrorCS"),sQuery(id+"F15.wireOp",EDGE,"E356.MirrorCS"),sQuery(id+"F15.wireOp",EDGE,"E357.MirrorCS"),sQuery(id+"F15.wireOp",EDGE,"E358.MirrorCS"),sQuery(id+"F15.wireOp",EDGE,"E360"),sQuery(id+"F15.wireOp",EDGE,"E362"),sQuery(id+"F15.wireOp",EDGE,"E363"),sQuery(id+"F15.wireOp",EDGE,"E364"),sQuery(id+"F15.wireOp",EDGE,"E366"),sQuery(id+"F15.wireOp",EDGE,"E368.MirrorCS"),sQuery(id+"F15.wireOp",EDGE,"E369.MirrorCS"),sQuery(id+"F15.wireOp",EDGE,"E370.MirrorCS"),sQuery(id+"F15.wireOp",EDGE,"E371.MirrorCS"),sQuery(id+"F15.wireOp",EDGE,"E372.MirrorCS"),sQuery(id+"F15.wireOp",EDGE,"E373.MirrorCS"),sQuery(id+"F15.wireOp",EDGE,"E374.MirrorCS"),sQuery(id+"F15.wireOp",EDGE,"E375.MirrorCS"),sQuery(id+"F15.wireOp",EDGE,"E377.MirrorCS"),sQuery(id+"F15.wireOp",EDGE,"E379.MirrorCS"),sQuery(id+"F15.wireOp",EDGE,"E380.MirrorCS"),sQuery(id+"F15.wireOp",EDGE,"E381.MirrorCS"),sQuery(id+"F15.wireOp",EDGE,"E382.MirrorCS"),sQuery(id+"F15.wireOp",EDGE,"E383.MirrorCS"),sQuery(id+"F15.wireOp",EDGE,"E384.MirrorCS"),sQuery(id+"F15.wireOp",EDGE,"E385.MirrorCS"),sQuery(id+"F15.wireOp",EDGE,"E386.MirrorCS"),sQuery(id+"F15.wireOp",EDGE,"E387.MirrorCS"),sQuery(id+"F15.wireOp",EDGE,"E388.MirrorCS"),sQuery(id+"F15.wireOp",EDGE,"E389.MirrorCS"),sQuery(id+"F15.wireOp",EDGE,"E390.MirrorCS"),sQuery(id+"F15.wireOp",EDGE,"E391.MirrorCS"),sQuery(id+"F15.wireOp",EDGE,"E394.MirrorCS"),sQuery(id+"F15.wireOp",EDGE,"E396.MirrorCS"),sQuery(id+"F15.wireOp",EDGE,"E397.MirrorCS"),sQuery(id+"F15.wireOp",EDGE,"E399.MirrorCS"),sQuery(id+"F15.wireOp",EDGE,"E402.MirrorCS"),sQuery(id+"F15.wireOp",EDGE,"E403.MirrorCS"),sQuery(id+"F15.wireOp",EDGE,"E405.MirrorCS"),sQuery(id+"F15.wireOp",EDGE,"E406.MirrorCS"),sQuery(id+"F15.wireOp",EDGE,"E409.MirrorCS"),sQuery(id+"F15.wireOp",EDGE,"E413.MirrorCS"),sQuery(id+"F15.wireOp",EDGE,"E414.MirrorCS"),sQuery(id+"F15.wireOp",EDGE,"E417.MirrorCS"),sQuery(id+"F15.wireOp",EDGE,"E418.MirrorCS"),sQuery(id+"F15.wireOp",EDGE,"E420.MirrorCS"),sQuery(id+"F15.wireOp",EDGE,"E421.MirrorCS"),sQuery(id+"F15.wireOp",EDGE,"E423.MirrorCS"),sQuery(id+"F15.wireOp",EDGE,"E427.MirrorCS"),sQuery(id+"F15.wireOp",EDGE,"E429.MirrorCS"),sQuery(id+"F15.wireOp",EDGE,"E431.MirrorCS"),sQuery(id+"F15.wireOp",EDGE,"E432.MirrorCS"),sQuery(id+"F15.wireOp",EDGE,"E433.MirrorCS"),sQuery(id+"F15.wireOp",EDGE,"E434.MirrorCS"),sQuery(id+"F15.wireOp",EDGE,"E436.MirrorCS"),sQuery(id+"F15.wireOp",EDGE,"E437.MirrorCS"),sQuery(id+"F15.wireOp",EDGE,"E438.MirrorCS")])],"isStart":false})]});
            var sketch = newSketch(context, id + "F25", { "sketchPlane" : qUnion([Q0])});
            skLineSegment(sketch, "E476.0", {"start": v(-52, -9.04) * mm, "end": v(-50.63, -17.4) * mm});
            skLineSegment(sketch, "E477.0", {"start": v(-52, -25.77) * mm, "end": v(-50.63, -17.4) * mm});
            skLineSegment(sketch, "E478.0", {"start": v(16.99, -9.05) * mm, "end": v(15.6, -17.4) * mm});
            skLineSegment(sketch, "E479.0", {"start": v(16.99, -25.76) * mm, "end": v(15.6, -17.4) * mm});
            skLineSegment(sketch, "E480", {"start": v(-52, -9.04) * mm, "end": v(-52, -25.77) * mm});
            skLineSegment(sketch, "E481", {"start": v(16.99, -9.05) * mm, "end": v(16.99, -25.76) * mm});
            skSolve(sketch);
        }
        {
            var Q0;
            Q0 = qSketchRegion(id + "F25", true);
            extrude(context, id + "F26", {"entities" : qUnion([Q0]), "operationType" : NewBodyOperationType.REMOVE, "endBound" : BoundingType.THROUGH_ALL, "oppositeDirection" : true, "depth" : 25.4 * mm, "offsetDistance" : 25.4 * mm});
        }
    });
